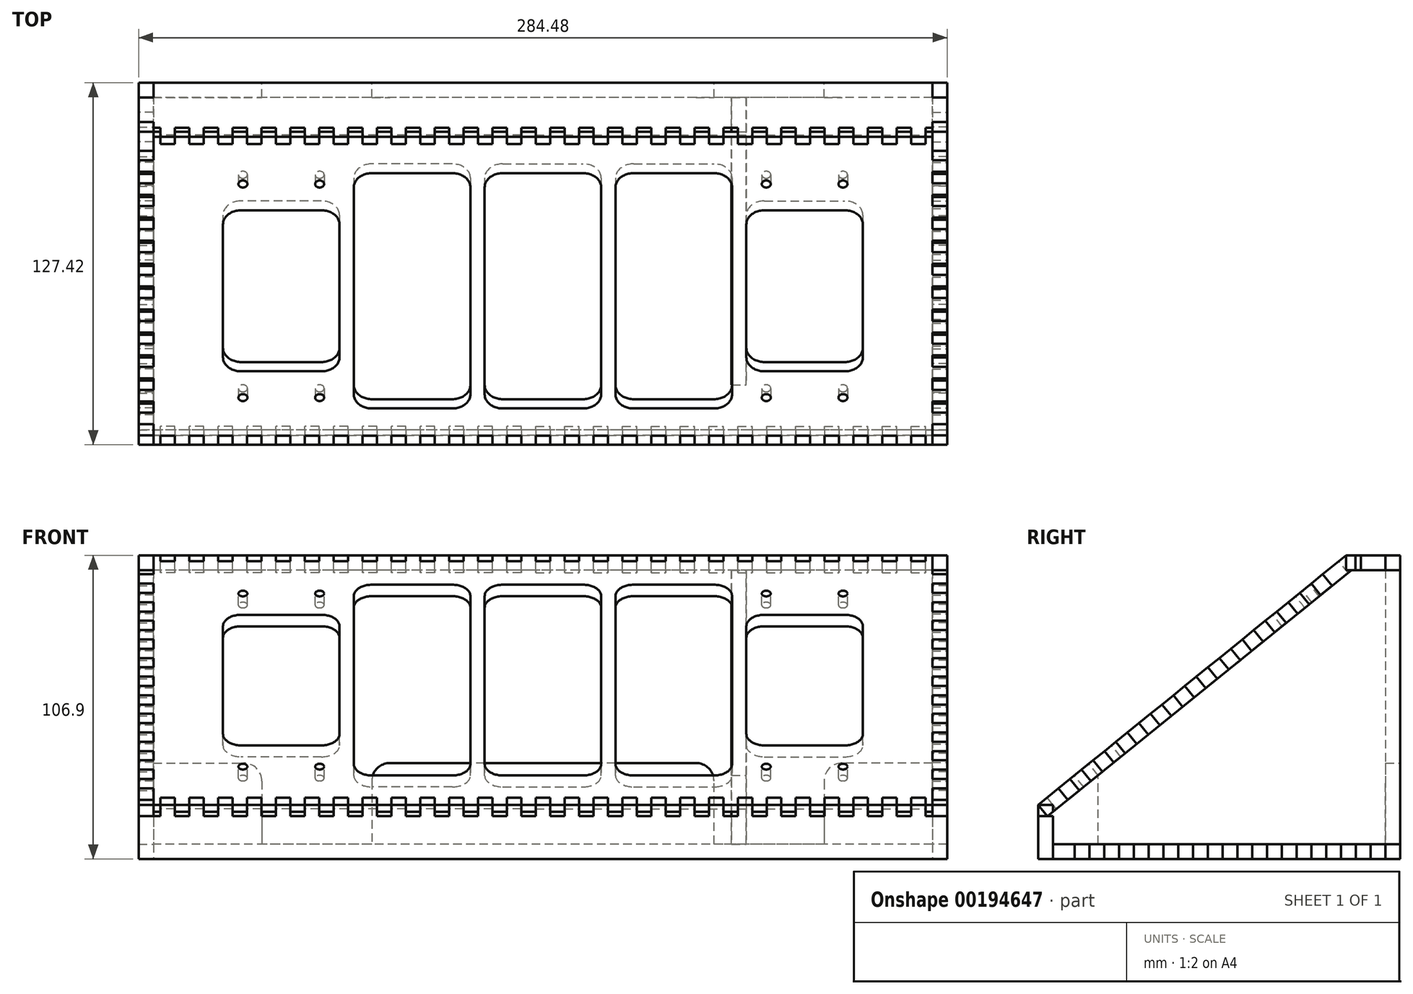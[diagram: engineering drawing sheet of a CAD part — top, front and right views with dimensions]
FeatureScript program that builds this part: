
annotation { "Feature Type Name" : "Feature", "Feature Type Description" : "" }
export const myFeature = defineFeature(function(context is Context, id is Id, definition is map)
    precondition{}
    {
        {
            var Q0;
            Q0=qCreatedBy(makeId("Right.planeOp"),FACE);
            var sketch = newSketch(context, id + "F0", { "sketchPlane" : qUnion([Q0])});
            skLineSegment(sketch, "E0.bottom", {"start": v(61.11, -2.6) * mm, "end": v(-61.11, -2.6) * mm});
            skLineSegment(sketch, "E0.top", {"start": v(61.11, 2.6) * mm, "end": v(-61.11, 2.6) * mm});
            skLineSegment(sketch, "E0.left", {"start": v(61.11, -2.6) * mm, "end": v(61.11, 2.6) * mm});
            skLineSegment(sketch, "E0.right", {"start": v(-61.11, -2.6) * mm, "end": v(-61.11, 2.6) * mm});
            skPoint(sketch, "E0.middle", {"position": v(0, 0) * mm});
            skLineSegment(sketch, "E1.bottom", {"start": v(-66.31, 16.45) * mm, "end": v(42.06, 104.3) * mm});
            skLineSegment(sketch, "E1.top", {"start": v(-63.04, 12.41) * mm, "end": v(45.34, 100.26) * mm});
            skLineSegment(sketch, "E1.left", {"start": v(-66.31, 16.45) * mm, "end": v(-63.04, 12.41) * mm});
            skLineSegment(sketch, "E1.right", {"start": v(42.06, 104.3) * mm, "end": v(45.34, 100.26) * mm});
            skLineSegment(sketch, "E2.bottom", {"start": v(-66.31, 16.45) * mm, "end": v(-61.11, 16.45) * mm});
            skLineSegment(sketch, "E2.top", {"start": v(-66.31, -2.6) * mm, "end": v(-61.11, -2.6) * mm});
            skLineSegment(sketch, "E2.left", {"start": v(-66.31, 16.45) * mm, "end": v(-66.31, -2.6) * mm});
            skLineSegment(sketch, "E2.right", {"start": v(-61.11, 16.45) * mm, "end": v(-61.11, -2.6) * mm});
            skLineSegment(sketch, "E3.bottom", {"start": v(-63.68, 26.3) * mm, "end": v(31.87, 103.76) * mm, "construction": true});
            skLineSegment(sketch, "E3.top", {"start": v(-59.9, 21.65) * mm, "end": v(35.65, 99.1) * mm, "construction": true});
            skLineSegment(sketch, "E3.left", {"start": v(-63.68, 26.3) * mm, "end": v(-59.9, 21.65) * mm, "construction": true});
            skLineSegment(sketch, "E3.right", {"start": v(31.87, 103.76) * mm, "end": v(35.65, 99.1) * mm, "construction": true});
            skLineSegment(sketch, "E4.bottom", {"start": v(42.06, 104.3) * mm, "end": v(61.11, 104.3) * mm});
            skLineSegment(sketch, "E4.top", {"start": v(42.06, 99.1) * mm, "end": v(61.11, 99.1) * mm});
            skLineSegment(sketch, "E4.left", {"start": v(42.06, 104.3) * mm, "end": v(42.06, 99.1) * mm});
            skLineSegment(sketch, "E4.right", {"start": v(61.11, 104.3) * mm, "end": v(61.11, 99.1) * mm});
            skLineSegment(sketch, "E5.bottom", {"start": v(61.11, 99.1) * mm, "end": v(55.91, 99.1) * mm});
            skLineSegment(sketch, "E5.top", {"start": v(61.11, 2.6) * mm, "end": v(55.91, 2.6) * mm});
            skLineSegment(sketch, "E5.left", {"start": v(61.11, 99.1) * mm, "end": v(61.11, 2.6) * mm});
            skLineSegment(sketch, "E5.right", {"start": v(55.91, 99.1) * mm, "end": v(55.91, 2.6) * mm});
            skLineSegment(sketch, "E6.bottom", {"start": v(-42.32, 43.63) * mm, "end": v(10.51, 86.44) * mm, "construction": true});
            skLineSegment(sketch, "E6.top", {"start": v(-15.24, 10.22) * mm, "end": v(37.59, 53.04) * mm, "construction": true});
            skLineSegment(sketch, "E6.left", {"start": v(-42.32, 43.63) * mm, "end": v(-15.24, 10.22) * mm, "construction": true});
            skLineSegment(sketch, "E6.right", {"start": v(10.51, 86.44) * mm, "end": v(37.59, 53.04) * mm, "construction": true});
            skPoint(sketch, "E7", {"position": v(-15.9, 65.03) * mm});
            skLineSegment(sketch, "E8", {"start": v(-63.18, 19) * mm, "end": v(-59.9, 14.95) * mm, "construction": true});
            skLineSegment(sketch, "E9", {"start": v(-66.31, 12.41) * mm, "end": v(-61.11, 12.41) * mm, "construction": true});
            skLineSegment(sketch, "E10", {"start": v(45.34, 104.3) * mm, "end": v(45.34, 99.1) * mm, "construction": true});
            skLineSegment(sketch, "E11", {"start": v(39.52, 102.23) * mm, "end": v(42.8, 98.2) * mm, "construction": true});
            skSolve(sketch);
        }
        {
            var Q0;
            Q0=qCreatedBy(makeId("Right.planeOp"),FACE);
            var sketch = newSketch(context, id + "F1", { "sketchPlane" : qUnion([Q0])});
            skLineSegment(sketch, "E12.0", {"start": v(-63.04, 12.41) * mm, "end": v(45.34, 100.26) * mm});
            skLineSegment(sketch, "E12.1", {"start": v(-66.31, 16.45) * mm, "end": v(-63.04, 12.41) * mm});
            skLineSegment(sketch, "E12.2", {"start": v(-66.31, 16.45) * mm, "end": v(42.06, 104.3) * mm});
            skLineSegment(sketch, "E12.3", {"start": v(42.06, 104.3) * mm, "end": v(45.34, 100.26) * mm});
            skSolve(sketch);
        }
        {
            var Q0;
            Q0 = qSketchRegion(id + "F1", true);
            extrude(context, id + "F2", {"entities" : qUnion([Q0]), "depth" : 142.24 * mm, "hasSecondDirection" : true, "secondDirectionOppositeDirection" : true, "secondDirectionDepth" : 142.24 * mm});
        }
        {
            var Q0;
            Q0=makeQuery(id+"F2.opExtrude","SWEPT_FACE",FACE,{"disambiguationData":[OSD([sQuery(id+"F1.wireOp",EDGE,"E12.2")])]});
            var sketch = newSketch(context, id + "F3", { "sketchPlane" : qUnion([Q0])});
            skLineSegment(sketch, "E13.bottom", {"start": v(-2.54, -41.16) * mm, "end": v(2.54, -41.16) * mm});
            skLineSegment(sketch, "E13.top", {"start": v(-2.54, -37.12) * mm, "end": v(2.54, -37.12) * mm});
            skLineSegment(sketch, "E13.left", {"start": v(2.54, -41.16) * mm, "end": v(2.54, -37.12) * mm});
            skLineSegment(sketch, "E13.right", {"start": v(-2.54, -41.16) * mm, "end": v(-2.54, -37.12) * mm});
            skPoint(sketch, "E14", {"position": v(0, -37.12) * mm});
            skLineSegment(sketch, "E15.1.0.0", {"start": v(7.62, -41.16) * mm, "end": v(7.62, -37.12) * mm});
            skLineSegment(sketch, "E15.1.0.1", {"start": v(12.7, -41.16) * mm, "end": v(12.7, -37.12) * mm});
            skLineSegment(sketch, "E15.1.0.2", {"start": v(7.62, -37.12) * mm, "end": v(12.7, -37.12) * mm});
            skLineSegment(sketch, "E15.1.0.3", {"start": v(7.62, -41.16) * mm, "end": v(12.7, -41.16) * mm});
            skLineSegment(sketch, "E15.2.0.0", {"start": v(17.78, -41.16) * mm, "end": v(17.78, -37.12) * mm});
            skLineSegment(sketch, "E15.2.0.1", {"start": v(22.86, -41.16) * mm, "end": v(22.86, -37.12) * mm});
            skLineSegment(sketch, "E15.2.0.2", {"start": v(17.78, -37.12) * mm, "end": v(22.86, -37.12) * mm});
            skLineSegment(sketch, "E15.2.0.3", {"start": v(17.78, -41.16) * mm, "end": v(22.86, -41.16) * mm});
            skLineSegment(sketch, "E15.3.0.0", {"start": v(27.94, -41.16) * mm, "end": v(27.94, -37.12) * mm});
            skLineSegment(sketch, "E15.3.0.1", {"start": v(33.02, -41.16) * mm, "end": v(33.02, -37.12) * mm});
            skLineSegment(sketch, "E15.3.0.2", {"start": v(27.94, -37.12) * mm, "end": v(33.02, -37.12) * mm});
            skLineSegment(sketch, "E15.3.0.3", {"start": v(27.94, -41.16) * mm, "end": v(33.02, -41.16) * mm});
            skLineSegment(sketch, "E15.4.0.0", {"start": v(38.1, -41.16) * mm, "end": v(38.1, -37.12) * mm});
            skLineSegment(sketch, "E15.4.0.1", {"start": v(43.18, -41.16) * mm, "end": v(43.18, -37.12) * mm});
            skLineSegment(sketch, "E15.4.0.2", {"start": v(38.1, -37.12) * mm, "end": v(43.18, -37.12) * mm});
            skLineSegment(sketch, "E15.4.0.3", {"start": v(38.1, -41.16) * mm, "end": v(43.18, -41.16) * mm});
            skLineSegment(sketch, "E15.5.0.0", {"start": v(48.26, -41.16) * mm, "end": v(48.26, -37.12) * mm});
            skLineSegment(sketch, "E15.5.0.1", {"start": v(53.34, -41.16) * mm, "end": v(53.34, -37.12) * mm});
            skLineSegment(sketch, "E15.5.0.2", {"start": v(48.26, -37.12) * mm, "end": v(53.34, -37.12) * mm});
            skLineSegment(sketch, "E15.5.0.3", {"start": v(48.26, -41.16) * mm, "end": v(53.34, -41.16) * mm});
            skLineSegment(sketch, "E15.6.0.0", {"start": v(58.42, -41.16) * mm, "end": v(58.42, -37.12) * mm});
            skLineSegment(sketch, "E15.6.0.1", {"start": v(63.5, -41.16) * mm, "end": v(63.5, -37.12) * mm});
            skLineSegment(sketch, "E15.6.0.2", {"start": v(58.42, -37.12) * mm, "end": v(63.5, -37.12) * mm});
            skLineSegment(sketch, "E15.6.0.3", {"start": v(58.42, -41.16) * mm, "end": v(63.5, -41.16) * mm});
            skLineSegment(sketch, "E15.7.0.0", {"start": v(68.58, -41.16) * mm, "end": v(68.58, -37.12) * mm});
            skLineSegment(sketch, "E15.7.0.1", {"start": v(73.66, -41.16) * mm, "end": v(73.66, -37.12) * mm});
            skLineSegment(sketch, "E15.7.0.2", {"start": v(68.58, -37.12) * mm, "end": v(73.66, -37.12) * mm});
            skLineSegment(sketch, "E15.7.0.3", {"start": v(68.58, -41.16) * mm, "end": v(73.66, -41.16) * mm});
            skLineSegment(sketch, "E15.8.0.0", {"start": v(78.74, -41.16) * mm, "end": v(78.74, -37.12) * mm});
            skLineSegment(sketch, "E15.8.0.1", {"start": v(83.82, -41.16) * mm, "end": v(83.82, -37.12) * mm});
            skLineSegment(sketch, "E15.8.0.2", {"start": v(78.74, -37.12) * mm, "end": v(83.82, -37.12) * mm});
            skLineSegment(sketch, "E15.8.0.3", {"start": v(78.74, -41.16) * mm, "end": v(83.82, -41.16) * mm});
            skLineSegment(sketch, "E15.9.0.0", {"start": v(88.9, -41.16) * mm, "end": v(88.9, -37.12) * mm});
            skLineSegment(sketch, "E15.9.0.1", {"start": v(93.98, -41.16) * mm, "end": v(93.98, -37.12) * mm});
            skLineSegment(sketch, "E15.9.0.2", {"start": v(88.9, -37.12) * mm, "end": v(93.98, -37.12) * mm});
            skLineSegment(sketch, "E15.9.0.3", {"start": v(88.9, -41.16) * mm, "end": v(93.98, -41.16) * mm});
            skLineSegment(sketch, "E15.10.0.0", {"start": v(99.06, -41.16) * mm, "end": v(99.06, -37.12) * mm});
            skLineSegment(sketch, "E15.10.0.1", {"start": v(104.14, -41.16) * mm, "end": v(104.14, -37.12) * mm});
            skLineSegment(sketch, "E15.10.0.2", {"start": v(99.06, -37.12) * mm, "end": v(104.14, -37.12) * mm});
            skLineSegment(sketch, "E15.10.0.3", {"start": v(99.06, -41.16) * mm, "end": v(104.14, -41.16) * mm});
            skLineSegment(sketch, "E15.11.0.0", {"start": v(109.22, -41.16) * mm, "end": v(109.22, -37.12) * mm});
            skLineSegment(sketch, "E15.11.0.1", {"start": v(114.3, -41.16) * mm, "end": v(114.3, -37.12) * mm});
            skLineSegment(sketch, "E15.11.0.2", {"start": v(109.22, -37.12) * mm, "end": v(114.3, -37.12) * mm});
            skLineSegment(sketch, "E15.11.0.3", {"start": v(109.22, -41.16) * mm, "end": v(114.3, -41.16) * mm});
            skLineSegment(sketch, "E15.12.0.0", {"start": v(119.38, -41.16) * mm, "end": v(119.38, -37.12) * mm});
            skLineSegment(sketch, "E15.12.0.1", {"start": v(124.46, -41.16) * mm, "end": v(124.46, -37.12) * mm});
            skLineSegment(sketch, "E15.12.0.2", {"start": v(119.38, -37.12) * mm, "end": v(124.46, -37.12) * mm});
            skLineSegment(sketch, "E15.12.0.3", {"start": v(119.38, -41.16) * mm, "end": v(124.46, -41.16) * mm});
            skLineSegment(sketch, "E15.13.0.0", {"start": v(129.54, -41.16) * mm, "end": v(129.54, -37.12) * mm});
            skLineSegment(sketch, "E15.13.0.1", {"start": v(134.62, -41.16) * mm, "end": v(134.62, -37.12) * mm});
            skLineSegment(sketch, "E15.13.0.2", {"start": v(129.54, -37.12) * mm, "end": v(134.62, -37.12) * mm});
            skLineSegment(sketch, "E15.13.0.3", {"start": v(129.54, -41.16) * mm, "end": v(134.62, -41.16) * mm});
            skLineSegment(sketch, "E15.direction1", {"start": v(-2.54, -41.16) * mm, "end": v(7.62, -41.16) * mm, "construction": true});
            skLineSegment(sketch, "E16.MirrorCS", {"start": v(-109.22, -41.16) * mm, "end": v(-109.22, -37.12) * mm});
            skLineSegment(sketch, "E17.MirrorCS", {"start": v(-68.58, -41.16) * mm, "end": v(-68.58, -37.12) * mm});
            skLineSegment(sketch, "E18.MirrorCS", {"start": v(-109.22, -37.12) * mm, "end": v(-114.3, -37.12) * mm});
            skLineSegment(sketch, "E19.MirrorCS", {"start": v(-114.3, -41.16) * mm, "end": v(-114.3, -37.12) * mm});
            skLineSegment(sketch, "E20.MirrorCS", {"start": v(-73.66, -41.16) * mm, "end": v(-73.66, -37.12) * mm});
            skLineSegment(sketch, "E21.MirrorCS", {"start": v(-68.58, -37.12) * mm, "end": v(-73.66, -37.12) * mm});
            skLineSegment(sketch, "E22.MirrorCS", {"start": v(-109.22, -41.16) * mm, "end": v(-114.3, -41.16) * mm});
            skLineSegment(sketch, "E23.MirrorCS", {"start": v(-68.58, -41.16) * mm, "end": v(-73.66, -41.16) * mm});
            skLineSegment(sketch, "E24.MirrorCS", {"start": v(-119.38, -41.16) * mm, "end": v(-119.38, -37.12) * mm});
            skLineSegment(sketch, "E25.MirrorCS", {"start": v(-78.74, -41.16) * mm, "end": v(-78.74, -37.12) * mm});
            skLineSegment(sketch, "E26.MirrorCS", {"start": v(-38.1, -41.16) * mm, "end": v(-38.1, -37.12) * mm});
            skLineSegment(sketch, "E27.MirrorCS", {"start": v(-124.46, -41.16) * mm, "end": v(-124.46, -37.12) * mm});
            skLineSegment(sketch, "E28.MirrorCS", {"start": v(-83.82, -41.16) * mm, "end": v(-83.82, -37.12) * mm});
            skLineSegment(sketch, "E29.MirrorCS", {"start": v(-43.18, -41.16) * mm, "end": v(-43.18, -37.12) * mm});
            skLineSegment(sketch, "E30.MirrorCS", {"start": v(-119.38, -37.12) * mm, "end": v(-124.46, -37.12) * mm});
            skLineSegment(sketch, "E31.MirrorCS", {"start": v(-78.74, -37.12) * mm, "end": v(-83.82, -37.12) * mm});
            skLineSegment(sketch, "E32.MirrorCS", {"start": v(-38.1, -37.12) * mm, "end": v(-43.18, -37.12) * mm});
            skLineSegment(sketch, "E33.MirrorCS", {"start": v(-119.38, -41.16) * mm, "end": v(-124.46, -41.16) * mm});
            skLineSegment(sketch, "E34.MirrorCS", {"start": v(-78.74, -41.16) * mm, "end": v(-83.82, -41.16) * mm});
            skLineSegment(sketch, "E35.MirrorCS", {"start": v(-38.1, -41.16) * mm, "end": v(-43.18, -41.16) * mm});
            skLineSegment(sketch, "E36.MirrorCS", {"start": v(-144.78, -41.16) * mm, "end": v(-144.78, -37.12) * mm});
            skLineSegment(sketch, "E37.MirrorCS", {"start": v(-63.5, -41.16) * mm, "end": v(-63.5, -37.12) * mm});
            skLineSegment(sketch, "E38.MirrorCS", {"start": v(-27.94, -41.16) * mm, "end": v(-27.94, -37.12) * mm});
            skLineSegment(sketch, "E39.MirrorCS", {"start": v(-104.14, -41.16) * mm, "end": v(-104.14, -37.12) * mm});
            skLineSegment(sketch, "E40.MirrorCS", {"start": v(-17.78, -41.16) * mm, "end": v(-22.86, -41.16) * mm});
            skLineSegment(sketch, "E41.MirrorCS", {"start": v(-17.78, -37.12) * mm, "end": v(-22.86, -37.12) * mm});
            skLineSegment(sketch, "E42.MirrorCS", {"start": v(-22.86, -41.16) * mm, "end": v(-22.86, -37.12) * mm});
            skLineSegment(sketch, "E43.MirrorCS", {"start": v(-129.54, -41.16) * mm, "end": v(-129.54, -37.12) * mm});
            skLineSegment(sketch, "E44.MirrorCS", {"start": v(-88.9, -41.16) * mm, "end": v(-88.9, -37.12) * mm});
            skLineSegment(sketch, "E45.MirrorCS", {"start": v(-17.78, -41.16) * mm, "end": v(-17.78, -37.12) * mm});
            skLineSegment(sketch, "E46.MirrorCS", {"start": v(-7.62, -41.16) * mm, "end": v(-12.7, -41.16) * mm});
            skLineSegment(sketch, "E47.MirrorCS", {"start": v(-7.62, -37.12) * mm, "end": v(-12.7, -37.12) * mm});
            skLineSegment(sketch, "E48.MirrorCS", {"start": v(-48.26, -41.16) * mm, "end": v(-48.26, -37.12) * mm});
            skLineSegment(sketch, "E49.MirrorCS", {"start": v(-139.7, -41.16) * mm, "end": v(-139.7, -37.12) * mm});
            skLineSegment(sketch, "E50.MirrorCS", {"start": v(-58.42, -41.16) * mm, "end": v(-58.42, -37.12) * mm});
            skLineSegment(sketch, "E51.MirrorCS", {"start": v(-99.06, -41.16) * mm, "end": v(-99.06, -37.12) * mm});
            skLineSegment(sketch, "E52.MirrorCS", {"start": v(-12.7, -41.16) * mm, "end": v(-12.7, -37.12) * mm});
            skLineSegment(sketch, "E53.MirrorCS", {"start": v(-129.54, -41.16) * mm, "end": v(-134.62, -41.16) * mm});
            skLineSegment(sketch, "E54.MirrorCS", {"start": v(-7.62, -41.16) * mm, "end": v(-7.62, -37.12) * mm});
            skLineSegment(sketch, "E55.MirrorCS", {"start": v(-48.26, -41.16) * mm, "end": v(-53.34, -41.16) * mm});
            skLineSegment(sketch, "E56.MirrorCS", {"start": v(-88.9, -41.16) * mm, "end": v(-93.98, -41.16) * mm});
            skLineSegment(sketch, "E57.MirrorCS", {"start": v(-139.7, -41.16) * mm, "end": v(-144.78, -41.16) * mm});
            skLineSegment(sketch, "E58.MirrorCS", {"start": v(-58.42, -41.16) * mm, "end": v(-63.5, -41.16) * mm});
            skLineSegment(sketch, "E59.MirrorCS", {"start": v(-99.06, -41.16) * mm, "end": v(-104.14, -41.16) * mm});
            skLineSegment(sketch, "E60.MirrorCS", {"start": v(-48.26, -37.12) * mm, "end": v(-53.34, -37.12) * mm});
            skLineSegment(sketch, "E61.MirrorCS", {"start": v(-88.9, -37.12) * mm, "end": v(-93.98, -37.12) * mm});
            skLineSegment(sketch, "E62.MirrorCS", {"start": v(-27.94, -41.16) * mm, "end": v(-33.02, -41.16) * mm});
            skLineSegment(sketch, "E63.MirrorCS", {"start": v(-139.7, -37.12) * mm, "end": v(-144.78, -37.12) * mm});
            skLineSegment(sketch, "E64.MirrorCS", {"start": v(-129.54, -37.12) * mm, "end": v(-134.62, -37.12) * mm});
            skLineSegment(sketch, "E65.MirrorCS", {"start": v(-27.94, -37.12) * mm, "end": v(-33.02, -37.12) * mm});
            skLineSegment(sketch, "E66.MirrorCS", {"start": v(-93.98, -41.16) * mm, "end": v(-93.98, -37.12) * mm});
            skLineSegment(sketch, "E67.MirrorCS", {"start": v(-53.34, -41.16) * mm, "end": v(-53.34, -37.12) * mm});
            skLineSegment(sketch, "E68.MirrorCS", {"start": v(-134.62, -41.16) * mm, "end": v(-134.62, -37.12) * mm});
            skLineSegment(sketch, "E69.MirrorCS", {"start": v(-99.06, -37.12) * mm, "end": v(-104.14, -37.12) * mm});
            skLineSegment(sketch, "E70.MirrorCS", {"start": v(-33.02, -41.16) * mm, "end": v(-33.02, -37.12) * mm});
            skLineSegment(sketch, "E71.MirrorCS", {"start": v(-58.42, -37.12) * mm, "end": v(-63.5, -37.12) * mm});
            skLineSegment(sketch, "E72", {"start": v(-142.24, 28.6) * mm, "end": v(142.24, 28.6) * mm, "construction": true});
            skLineSegment(sketch, "E73.bottom", {"start": v(-2.54, 98.35) * mm, "end": v(2.54, 98.35) * mm});
            skLineSegment(sketch, "E73.top", {"start": v(-2.54, 95.07) * mm, "end": v(2.54, 95.07) * mm});
            skLineSegment(sketch, "E73.left", {"start": v(-2.54, 98.35) * mm, "end": v(-2.54, 95.07) * mm});
            skLineSegment(sketch, "E73.right", {"start": v(2.54, 98.35) * mm, "end": v(2.54, 95.07) * mm});
            skPoint(sketch, "E74", {"position": v(0, 95.07) * mm});
            skLineSegment(sketch, "E75.0.14.0", {"start": v(139.7, -41.16) * mm, "end": v(139.7, -37.12) * mm});
            skLineSegment(sketch, "E75.3.14.0", {"start": v(144.78, -41.16) * mm, "end": v(144.78, -37.12) * mm});
            skLineSegment(sketch, "E75.6.14.0", {"start": v(139.7, -37.12) * mm, "end": v(144.78, -37.12) * mm});
            skLineSegment(sketch, "E75.9.14.0", {"start": v(139.7, -41.16) * mm, "end": v(144.78, -41.16) * mm});
            skLineSegment(sketch, "E76.1.0.0", {"start": v(12.7, 98.35) * mm, "end": v(12.7, 95.07) * mm});
            skLineSegment(sketch, "E76.1.0.1", {"start": v(7.62, 98.35) * mm, "end": v(12.7, 98.35) * mm});
            skLineSegment(sketch, "E76.1.0.2", {"start": v(7.62, 98.35) * mm, "end": v(7.62, 95.07) * mm});
            skLineSegment(sketch, "E76.1.0.3", {"start": v(7.62, 95.07) * mm, "end": v(12.7, 95.07) * mm});
            skLineSegment(sketch, "E76.2.0.0", {"start": v(22.86, 98.35) * mm, "end": v(22.86, 95.07) * mm});
            skLineSegment(sketch, "E76.2.0.1", {"start": v(17.78, 98.35) * mm, "end": v(22.86, 98.35) * mm});
            skLineSegment(sketch, "E76.2.0.2", {"start": v(17.78, 98.35) * mm, "end": v(17.78, 95.07) * mm});
            skLineSegment(sketch, "E76.2.0.3", {"start": v(17.78, 95.07) * mm, "end": v(22.86, 95.07) * mm});
            skLineSegment(sketch, "E76.3.0.0", {"start": v(33.02, 98.35) * mm, "end": v(33.02, 95.07) * mm});
            skLineSegment(sketch, "E76.3.0.1", {"start": v(27.94, 98.35) * mm, "end": v(33.02, 98.35) * mm});
            skLineSegment(sketch, "E76.3.0.2", {"start": v(27.94, 98.35) * mm, "end": v(27.94, 95.07) * mm});
            skLineSegment(sketch, "E76.3.0.3", {"start": v(27.94, 95.07) * mm, "end": v(33.02, 95.07) * mm});
            skLineSegment(sketch, "E76.4.0.0", {"start": v(43.18, 98.35) * mm, "end": v(43.18, 95.07) * mm});
            skLineSegment(sketch, "E76.4.0.1", {"start": v(38.1, 98.35) * mm, "end": v(43.18, 98.35) * mm});
            skLineSegment(sketch, "E76.4.0.2", {"start": v(38.1, 98.35) * mm, "end": v(38.1, 95.07) * mm});
            skLineSegment(sketch, "E76.4.0.3", {"start": v(38.1, 95.07) * mm, "end": v(43.18, 95.07) * mm});
            skLineSegment(sketch, "E76.5.0.0", {"start": v(53.34, 98.35) * mm, "end": v(53.34, 95.07) * mm});
            skLineSegment(sketch, "E76.5.0.1", {"start": v(48.26, 98.35) * mm, "end": v(53.34, 98.35) * mm});
            skLineSegment(sketch, "E76.5.0.2", {"start": v(48.26, 98.35) * mm, "end": v(48.26, 95.07) * mm});
            skLineSegment(sketch, "E76.5.0.3", {"start": v(48.26, 95.07) * mm, "end": v(53.34, 95.07) * mm});
            skLineSegment(sketch, "E76.6.0.0", {"start": v(63.5, 98.35) * mm, "end": v(63.5, 95.07) * mm});
            skLineSegment(sketch, "E76.6.0.1", {"start": v(58.42, 98.35) * mm, "end": v(63.5, 98.35) * mm});
            skLineSegment(sketch, "E76.6.0.2", {"start": v(58.42, 98.35) * mm, "end": v(58.42, 95.07) * mm});
            skLineSegment(sketch, "E76.6.0.3", {"start": v(58.42, 95.07) * mm, "end": v(63.5, 95.07) * mm});
            skLineSegment(sketch, "E76.7.0.0", {"start": v(73.66, 98.35) * mm, "end": v(73.66, 95.07) * mm});
            skLineSegment(sketch, "E76.7.0.1", {"start": v(68.58, 98.35) * mm, "end": v(73.66, 98.35) * mm});
            skLineSegment(sketch, "E76.7.0.2", {"start": v(68.58, 98.35) * mm, "end": v(68.58, 95.07) * mm});
            skLineSegment(sketch, "E76.7.0.3", {"start": v(68.58, 95.07) * mm, "end": v(73.66, 95.07) * mm});
            skLineSegment(sketch, "E76.8.0.0", {"start": v(83.82, 98.35) * mm, "end": v(83.82, 95.07) * mm});
            skLineSegment(sketch, "E76.8.0.1", {"start": v(78.74, 98.35) * mm, "end": v(83.82, 98.35) * mm});
            skLineSegment(sketch, "E76.8.0.2", {"start": v(78.74, 98.35) * mm, "end": v(78.74, 95.07) * mm});
            skLineSegment(sketch, "E76.8.0.3", {"start": v(78.74, 95.07) * mm, "end": v(83.82, 95.07) * mm});
            skLineSegment(sketch, "E76.9.0.0", {"start": v(93.98, 98.35) * mm, "end": v(93.98, 95.07) * mm});
            skLineSegment(sketch, "E76.9.0.1", {"start": v(88.9, 98.35) * mm, "end": v(93.98, 98.35) * mm});
            skLineSegment(sketch, "E76.9.0.2", {"start": v(88.9, 98.35) * mm, "end": v(88.9, 95.07) * mm});
            skLineSegment(sketch, "E76.9.0.3", {"start": v(88.9, 95.07) * mm, "end": v(93.98, 95.07) * mm});
            skLineSegment(sketch, "E76.10.0.0", {"start": v(104.14, 98.35) * mm, "end": v(104.14, 95.07) * mm});
            skLineSegment(sketch, "E76.10.0.1", {"start": v(99.06, 98.35) * mm, "end": v(104.14, 98.35) * mm});
            skLineSegment(sketch, "E76.10.0.2", {"start": v(99.06, 98.35) * mm, "end": v(99.06, 95.07) * mm});
            skLineSegment(sketch, "E76.10.0.3", {"start": v(99.06, 95.07) * mm, "end": v(104.14, 95.07) * mm});
            skLineSegment(sketch, "E76.11.0.0", {"start": v(114.3, 98.35) * mm, "end": v(114.3, 95.07) * mm});
            skLineSegment(sketch, "E76.11.0.1", {"start": v(109.22, 98.35) * mm, "end": v(114.3, 98.35) * mm});
            skLineSegment(sketch, "E76.11.0.2", {"start": v(109.22, 98.35) * mm, "end": v(109.22, 95.07) * mm});
            skLineSegment(sketch, "E76.11.0.3", {"start": v(109.22, 95.07) * mm, "end": v(114.3, 95.07) * mm});
            skLineSegment(sketch, "E76.12.0.0", {"start": v(124.46, 98.35) * mm, "end": v(124.46, 95.07) * mm});
            skLineSegment(sketch, "E76.12.0.1", {"start": v(119.38, 98.35) * mm, "end": v(124.46, 98.35) * mm});
            skLineSegment(sketch, "E76.12.0.2", {"start": v(119.38, 98.35) * mm, "end": v(119.38, 95.07) * mm});
            skLineSegment(sketch, "E76.12.0.3", {"start": v(119.38, 95.07) * mm, "end": v(124.46, 95.07) * mm});
            skLineSegment(sketch, "E76.13.0.0", {"start": v(134.62, 98.35) * mm, "end": v(134.62, 95.07) * mm});
            skLineSegment(sketch, "E76.13.0.1", {"start": v(129.54, 98.35) * mm, "end": v(134.62, 98.35) * mm});
            skLineSegment(sketch, "E76.13.0.2", {"start": v(129.54, 98.35) * mm, "end": v(129.54, 95.07) * mm});
            skLineSegment(sketch, "E76.13.0.3", {"start": v(129.54, 95.07) * mm, "end": v(134.62, 95.07) * mm});
            skLineSegment(sketch, "E76.14.0.0", {"start": v(144.78, 98.35) * mm, "end": v(144.78, 95.07) * mm});
            skLineSegment(sketch, "E76.14.0.1", {"start": v(139.7, 98.35) * mm, "end": v(144.78, 98.35) * mm});
            skLineSegment(sketch, "E76.14.0.2", {"start": v(139.7, 98.35) * mm, "end": v(139.7, 95.07) * mm});
            skLineSegment(sketch, "E76.14.0.3", {"start": v(139.7, 95.07) * mm, "end": v(144.78, 95.07) * mm});
            skLineSegment(sketch, "E76.direction1", {"start": v(-2.54, 95.07) * mm, "end": v(7.62, 95.07) * mm, "construction": true});
            skLineSegment(sketch, "E77.MirrorCS", {"start": v(-119.38, 95.07) * mm, "end": v(-124.46, 95.07) * mm});
            skLineSegment(sketch, "E78.MirrorCS", {"start": v(-68.58, 98.35) * mm, "end": v(-73.66, 98.35) * mm});
            skLineSegment(sketch, "E79.MirrorCS", {"start": v(-78.74, 98.35) * mm, "end": v(-78.74, 95.07) * mm});
            skLineSegment(sketch, "E80.MirrorCS", {"start": v(-27.94, 98.35) * mm, "end": v(-33.02, 98.35) * mm});
            skLineSegment(sketch, "E81.MirrorCS", {"start": v(-38.1, 98.35) * mm, "end": v(-38.1, 95.07) * mm});
            skLineSegment(sketch, "E82.MirrorCS", {"start": v(-27.94, 95.07) * mm, "end": v(-33.02, 95.07) * mm});
            skLineSegment(sketch, "E83.MirrorCS", {"start": v(-27.94, 98.35) * mm, "end": v(-27.94, 95.07) * mm});
            skLineSegment(sketch, "E84.MirrorCS", {"start": v(-68.58, 98.35) * mm, "end": v(-68.58, 95.07) * mm});
            skLineSegment(sketch, "E85.MirrorCS", {"start": v(-88.9, 98.35) * mm, "end": v(-88.9, 95.07) * mm});
            skLineSegment(sketch, "E86.MirrorCS", {"start": v(-129.54, 98.35) * mm, "end": v(-129.54, 95.07) * mm});
            skLineSegment(sketch, "E87.MirrorCS", {"start": v(-109.22, 98.35) * mm, "end": v(-109.22, 95.07) * mm});
            skLineSegment(sketch, "E88.MirrorCS", {"start": v(-124.46, 98.35) * mm, "end": v(-124.46, 95.07) * mm});
            skLineSegment(sketch, "E89.MirrorCS", {"start": v(-83.82, 98.35) * mm, "end": v(-83.82, 95.07) * mm});
            skLineSegment(sketch, "E90.MirrorCS", {"start": v(-43.18, 98.35) * mm, "end": v(-43.18, 95.07) * mm});
            skLineSegment(sketch, "E91.MirrorCS", {"start": v(-22.86, 98.35) * mm, "end": v(-22.86, 95.07) * mm});
            skLineSegment(sketch, "E92.MirrorCS", {"start": v(-48.26, 95.07) * mm, "end": v(-53.34, 95.07) * mm});
            skLineSegment(sketch, "E93.MirrorCS", {"start": v(-129.54, 95.07) * mm, "end": v(-134.62, 95.07) * mm});
            skLineSegment(sketch, "E94.MirrorCS", {"start": v(-88.9, 95.07) * mm, "end": v(-93.98, 95.07) * mm});
            skLineSegment(sketch, "E95.MirrorCS", {"start": v(-99.06, 98.35) * mm, "end": v(-104.14, 98.35) * mm});
            skLineSegment(sketch, "E96.MirrorCS", {"start": v(-48.26, 98.35) * mm, "end": v(-53.34, 98.35) * mm});
            skLineSegment(sketch, "E97.MirrorCS", {"start": v(-88.9, 98.35) * mm, "end": v(-93.98, 98.35) * mm});
            skLineSegment(sketch, "E98.MirrorCS", {"start": v(-7.62, 98.35) * mm, "end": v(-12.7, 98.35) * mm});
            skLineSegment(sketch, "E99.MirrorCS", {"start": v(-7.62, 95.07) * mm, "end": v(-12.7, 95.07) * mm});
            skLineSegment(sketch, "E100.MirrorCS", {"start": v(-119.38, 98.35) * mm, "end": v(-124.46, 98.35) * mm});
            skLineSegment(sketch, "E101.MirrorCS", {"start": v(-58.42, 98.35) * mm, "end": v(-58.42, 95.07) * mm});
            skLineSegment(sketch, "E102.MirrorCS", {"start": v(-63.5, 98.35) * mm, "end": v(-63.5, 95.07) * mm});
            skLineSegment(sketch, "E103.MirrorCS", {"start": v(-93.98, 98.35) * mm, "end": v(-93.98, 95.07) * mm});
            skLineSegment(sketch, "E104.MirrorCS", {"start": v(-134.62, 98.35) * mm, "end": v(-134.62, 95.07) * mm});
            skLineSegment(sketch, "E105.MirrorCS", {"start": v(-53.34, 98.35) * mm, "end": v(-53.34, 95.07) * mm});
            skLineSegment(sketch, "E106.MirrorCS", {"start": v(-38.1, 95.07) * mm, "end": v(-43.18, 95.07) * mm});
            skLineSegment(sketch, "E107.MirrorCS", {"start": v(-58.42, 98.35) * mm, "end": v(-63.5, 98.35) * mm});
            skLineSegment(sketch, "E108.MirrorCS", {"start": v(-114.3, 98.35) * mm, "end": v(-114.3, 95.07) * mm});
            skLineSegment(sketch, "E109.MirrorCS", {"start": v(-7.62, 98.35) * mm, "end": v(-7.62, 95.07) * mm});
            skLineSegment(sketch, "E110.MirrorCS", {"start": v(-68.58, 95.07) * mm, "end": v(-73.66, 95.07) * mm});
            skLineSegment(sketch, "E111.MirrorCS", {"start": v(-144.78, 98.35) * mm, "end": v(-144.78, 95.07) * mm});
            skLineSegment(sketch, "E112.MirrorCS", {"start": v(-38.1, 98.35) * mm, "end": v(-43.18, 98.35) * mm});
            skLineSegment(sketch, "E113.MirrorCS", {"start": v(-78.74, 98.35) * mm, "end": v(-83.82, 98.35) * mm});
            skLineSegment(sketch, "E114.MirrorCS", {"start": v(-48.26, 98.35) * mm, "end": v(-48.26, 95.07) * mm});
            skLineSegment(sketch, "E115.MirrorCS", {"start": v(-119.38, 98.35) * mm, "end": v(-119.38, 95.07) * mm});
            skLineSegment(sketch, "E116.MirrorCS", {"start": v(-33.02, 98.35) * mm, "end": v(-33.02, 95.07) * mm});
            skLineSegment(sketch, "E117.MirrorCS", {"start": v(-78.74, 95.07) * mm, "end": v(-83.82, 95.07) * mm});
            skLineSegment(sketch, "E118.MirrorCS", {"start": v(-129.54, 98.35) * mm, "end": v(-134.62, 98.35) * mm});
            skLineSegment(sketch, "E119.MirrorCS", {"start": v(-12.7, 98.35) * mm, "end": v(-12.7, 95.07) * mm});
            skLineSegment(sketch, "E120.MirrorCS", {"start": v(-73.66, 98.35) * mm, "end": v(-73.66, 95.07) * mm});
            skLineSegment(sketch, "E121.MirrorCS", {"start": v(-17.78, 98.35) * mm, "end": v(-17.78, 95.07) * mm});
            skLineSegment(sketch, "E122.MirrorCS", {"start": v(-99.06, 98.35) * mm, "end": v(-99.06, 95.07) * mm});
            skLineSegment(sketch, "E123.MirrorCS", {"start": v(-99.06, 95.07) * mm, "end": v(-104.14, 95.07) * mm});
            skLineSegment(sketch, "E124.MirrorCS", {"start": v(-58.42, 95.07) * mm, "end": v(-63.5, 95.07) * mm});
            skLineSegment(sketch, "E125.MirrorCS", {"start": v(-17.78, 95.07) * mm, "end": v(-22.86, 95.07) * mm});
            skLineSegment(sketch, "E126.MirrorCS", {"start": v(-139.7, 98.35) * mm, "end": v(-139.7, 95.07) * mm});
            skLineSegment(sketch, "E127.MirrorCS", {"start": v(-17.78, 98.35) * mm, "end": v(-22.86, 98.35) * mm});
            skLineSegment(sketch, "E128.MirrorCS", {"start": v(-104.14, 98.35) * mm, "end": v(-104.14, 95.07) * mm});
            skLineSegment(sketch, "E129.MirrorCS", {"start": v(-109.22, 98.35) * mm, "end": v(-114.3, 98.35) * mm});
            skLineSegment(sketch, "E130.MirrorCS", {"start": v(-109.22, 95.07) * mm, "end": v(-114.3, 95.07) * mm});
            skLineSegment(sketch, "E131.MirrorCS", {"start": v(-139.7, 98.35) * mm, "end": v(-144.78, 98.35) * mm});
            skLineSegment(sketch, "E132.MirrorCS", {"start": v(-139.7, 95.07) * mm, "end": v(-144.78, 95.07) * mm});
            skSolve(sketch);
        }
        {
            var Q0;
            Q0 = qSketchRegion(id + "F3", true);
            extrude(context, id + "F4", {"entities" : qUnion([Q0]), "operationType" : NewBodyOperationType.REMOVE, "endBound" : BoundingType.THROUGH_ALL, "oppositeDirection" : true, "depth" : 25.4 * mm});
        }
        {
            var Q0;
            Q0=qCreatedBy(makeId("Right.planeOp"),FACE);
            var sketch = newSketch(context, id + "F5", { "sketchPlane" : qUnion([Q0])});
            skLineSegment(sketch, "E133.0", {"start": v(-61.11, 16.45) * mm, "end": v(-61.11, -2.6) * mm});
            skLineSegment(sketch, "E133.1", {"start": v(-66.31, -2.6) * mm, "end": v(-61.11, -2.6) * mm});
            skLineSegment(sketch, "E133.2", {"start": v(-66.31, 16.45) * mm, "end": v(-66.31, -2.6) * mm});
            skLineSegment(sketch, "E133.3", {"start": v(-66.31, 16.45) * mm, "end": v(-61.11, 16.45) * mm});
            skSolve(sketch);
        }
        {
            var Q0;
            Q0 = qSketchRegion(id + "F5", true);
            extrude(context, id + "F6", {"entities" : qUnion([Q0]), "depth" : 142.24 * mm, "hasSecondDirection" : true, "secondDirectionOppositeDirection" : true, "secondDirectionDepth" : 142.24 * mm});
        }
        {
            var Q0;
            Q0=makeQuery(id+"F6.opExtrude","SWEPT_FACE",FACE,{"disambiguationData":[OSD([sQuery(id+"F5.wireOp",EDGE,"E133.2")])]});
            var sketch = newSketch(context, id + "F7", { "sketchPlane" : qUnion([Q0])});
            skLineSegment(sketch, "E134.bottom", {"start": v(2.54, 16.45) * mm, "end": v(7.62, 16.45) * mm});
            skLineSegment(sketch, "E134.top", {"start": v(2.54, 12.46) * mm, "end": v(7.62, 12.46) * mm});
            skLineSegment(sketch, "E134.left", {"start": v(2.54, 16.45) * mm, "end": v(2.54, 12.46) * mm});
            skLineSegment(sketch, "E134.right", {"start": v(7.62, 16.45) * mm, "end": v(7.62, 12.46) * mm});
            skLineSegment(sketch, "E135", {"start": v(2.54, 16.45) * mm, "end": v(-2.54, 16.45) * mm, "construction": true});
            skLineSegment(sketch, "E136.1.0.0", {"start": v(17.78, 16.45) * mm, "end": v(17.78, 12.46) * mm});
            skLineSegment(sketch, "E136.1.0.1", {"start": v(12.7, 16.45) * mm, "end": v(12.7, 12.46) * mm});
            skLineSegment(sketch, "E136.1.0.2", {"start": v(12.7, 12.46) * mm, "end": v(17.78, 12.46) * mm});
            skLineSegment(sketch, "E136.1.0.3", {"start": v(12.7, 16.45) * mm, "end": v(17.78, 16.45) * mm});
            skLineSegment(sketch, "E136.2.0.0", {"start": v(27.94, 16.45) * mm, "end": v(27.94, 12.46) * mm});
            skLineSegment(sketch, "E136.2.0.1", {"start": v(22.86, 16.45) * mm, "end": v(22.86, 12.46) * mm});
            skLineSegment(sketch, "E136.2.0.2", {"start": v(22.86, 12.46) * mm, "end": v(27.94, 12.46) * mm});
            skLineSegment(sketch, "E136.2.0.3", {"start": v(22.86, 16.45) * mm, "end": v(27.94, 16.45) * mm});
            skLineSegment(sketch, "E136.3.0.0", {"start": v(38.1, 16.45) * mm, "end": v(38.1, 12.46) * mm});
            skLineSegment(sketch, "E136.3.0.1", {"start": v(33.02, 16.45) * mm, "end": v(33.02, 12.46) * mm});
            skLineSegment(sketch, "E136.3.0.2", {"start": v(33.02, 12.46) * mm, "end": v(38.1, 12.46) * mm});
            skLineSegment(sketch, "E136.3.0.3", {"start": v(33.02, 16.45) * mm, "end": v(38.1, 16.45) * mm});
            skLineSegment(sketch, "E136.4.0.0", {"start": v(48.26, 16.45) * mm, "end": v(48.26, 12.46) * mm});
            skLineSegment(sketch, "E136.4.0.1", {"start": v(43.18, 16.45) * mm, "end": v(43.18, 12.46) * mm});
            skLineSegment(sketch, "E136.4.0.2", {"start": v(43.18, 12.46) * mm, "end": v(48.26, 12.46) * mm});
            skLineSegment(sketch, "E136.4.0.3", {"start": v(43.18, 16.45) * mm, "end": v(48.26, 16.45) * mm});
            skLineSegment(sketch, "E136.5.0.0", {"start": v(58.42, 16.45) * mm, "end": v(58.42, 12.46) * mm});
            skLineSegment(sketch, "E136.5.0.1", {"start": v(53.34, 16.45) * mm, "end": v(53.34, 12.46) * mm});
            skLineSegment(sketch, "E136.5.0.2", {"start": v(53.34, 12.46) * mm, "end": v(58.42, 12.46) * mm});
            skLineSegment(sketch, "E136.5.0.3", {"start": v(53.34, 16.45) * mm, "end": v(58.42, 16.45) * mm});
            skLineSegment(sketch, "E136.6.0.0", {"start": v(68.58, 16.45) * mm, "end": v(68.58, 12.46) * mm});
            skLineSegment(sketch, "E136.6.0.1", {"start": v(63.5, 16.45) * mm, "end": v(63.5, 12.46) * mm});
            skLineSegment(sketch, "E136.6.0.2", {"start": v(63.5, 12.46) * mm, "end": v(68.58, 12.46) * mm});
            skLineSegment(sketch, "E136.6.0.3", {"start": v(63.5, 16.45) * mm, "end": v(68.58, 16.45) * mm});
            skLineSegment(sketch, "E136.7.0.0", {"start": v(78.74, 16.45) * mm, "end": v(78.74, 12.46) * mm});
            skLineSegment(sketch, "E136.7.0.1", {"start": v(73.66, 16.45) * mm, "end": v(73.66, 12.46) * mm});
            skLineSegment(sketch, "E136.7.0.2", {"start": v(73.66, 12.46) * mm, "end": v(78.74, 12.46) * mm});
            skLineSegment(sketch, "E136.7.0.3", {"start": v(73.66, 16.45) * mm, "end": v(78.74, 16.45) * mm});
            skLineSegment(sketch, "E136.8.0.0", {"start": v(88.9, 16.45) * mm, "end": v(88.9, 12.46) * mm});
            skLineSegment(sketch, "E136.8.0.1", {"start": v(83.82, 16.45) * mm, "end": v(83.82, 12.46) * mm});
            skLineSegment(sketch, "E136.8.0.2", {"start": v(83.82, 12.46) * mm, "end": v(88.9, 12.46) * mm});
            skLineSegment(sketch, "E136.8.0.3", {"start": v(83.82, 16.45) * mm, "end": v(88.9, 16.45) * mm});
            skLineSegment(sketch, "E136.9.0.0", {"start": v(99.06, 16.45) * mm, "end": v(99.06, 12.46) * mm});
            skLineSegment(sketch, "E136.9.0.1", {"start": v(93.98, 16.45) * mm, "end": v(93.98, 12.46) * mm});
            skLineSegment(sketch, "E136.9.0.2", {"start": v(93.98, 12.46) * mm, "end": v(99.06, 12.46) * mm});
            skLineSegment(sketch, "E136.9.0.3", {"start": v(93.98, 16.45) * mm, "end": v(99.06, 16.45) * mm});
            skLineSegment(sketch, "E136.10.0.0", {"start": v(109.22, 16.45) * mm, "end": v(109.22, 12.46) * mm});
            skLineSegment(sketch, "E136.10.0.1", {"start": v(104.14, 16.45) * mm, "end": v(104.14, 12.46) * mm});
            skLineSegment(sketch, "E136.10.0.2", {"start": v(104.14, 12.46) * mm, "end": v(109.22, 12.46) * mm});
            skLineSegment(sketch, "E136.10.0.3", {"start": v(104.14, 16.45) * mm, "end": v(109.22, 16.45) * mm});
            skLineSegment(sketch, "E136.11.0.0", {"start": v(119.38, 16.45) * mm, "end": v(119.38, 12.46) * mm});
            skLineSegment(sketch, "E136.11.0.1", {"start": v(114.3, 16.45) * mm, "end": v(114.3, 12.46) * mm});
            skLineSegment(sketch, "E136.11.0.2", {"start": v(114.3, 12.46) * mm, "end": v(119.38, 12.46) * mm});
            skLineSegment(sketch, "E136.11.0.3", {"start": v(114.3, 16.45) * mm, "end": v(119.38, 16.45) * mm});
            skLineSegment(sketch, "E136.12.0.0", {"start": v(129.54, 16.45) * mm, "end": v(129.54, 12.46) * mm});
            skLineSegment(sketch, "E136.12.0.1", {"start": v(124.46, 16.45) * mm, "end": v(124.46, 12.46) * mm});
            skLineSegment(sketch, "E136.12.0.2", {"start": v(124.46, 12.46) * mm, "end": v(129.54, 12.46) * mm});
            skLineSegment(sketch, "E136.12.0.3", {"start": v(124.46, 16.45) * mm, "end": v(129.54, 16.45) * mm});
            skLineSegment(sketch, "E136.13.0.0", {"start": v(139.7, 16.45) * mm, "end": v(139.7, 12.46) * mm, "construction": true});
            skLineSegment(sketch, "E136.13.0.1", {"start": v(134.62, 16.45) * mm, "end": v(134.62, 12.46) * mm});
            skLineSegment(sketch, "E136.13.0.2", {"start": v(134.62, 12.46) * mm, "end": v(139.7, 12.46) * mm});
            skLineSegment(sketch, "E136.13.0.3", {"start": v(134.62, 16.45) * mm, "end": v(139.7, 16.45) * mm});
            skLineSegment(sketch, "E136.direction1", {"start": v(2.54, 12.46) * mm, "end": v(12.7, 12.46) * mm, "construction": true});
            skLineSegment(sketch, "E137.MirrorCS", {"start": v(-2.54, 16.45) * mm, "end": v(-2.54, 12.46) * mm});
            skLineSegment(sketch, "E138.MirrorCS", {"start": v(-2.54, 12.46) * mm, "end": v(-7.62, 12.46) * mm});
            skLineSegment(sketch, "E139.MirrorCS", {"start": v(-134.62, 12.46) * mm, "end": v(-139.7, 12.46) * mm});
            skLineSegment(sketch, "E140.MirrorCS", {"start": v(-53.34, 12.46) * mm, "end": v(-58.42, 12.46) * mm});
            skLineSegment(sketch, "E141.MirrorCS", {"start": v(-93.98, 12.46) * mm, "end": v(-99.06, 12.46) * mm});
            skLineSegment(sketch, "E142.MirrorCS", {"start": v(-33.02, 16.45) * mm, "end": v(-38.1, 16.45) * mm});
            skLineSegment(sketch, "E143.MirrorCS", {"start": v(-73.66, 16.45) * mm, "end": v(-78.74, 16.45) * mm});
            skLineSegment(sketch, "E144.MirrorCS", {"start": v(-114.3, 16.45) * mm, "end": v(-119.38, 16.45) * mm});
            skLineSegment(sketch, "E145.MirrorCS", {"start": v(-53.34, 16.45) * mm, "end": v(-53.34, 12.46) * mm});
            skLineSegment(sketch, "E146.MirrorCS", {"start": v(-73.66, 12.46) * mm, "end": v(-78.74, 12.46) * mm});
            skLineSegment(sketch, "E147.MirrorCS", {"start": v(-93.98, 16.45) * mm, "end": v(-93.98, 12.46) * mm});
            skLineSegment(sketch, "E148.MirrorCS", {"start": v(-114.3, 12.46) * mm, "end": v(-119.38, 12.46) * mm});
            skLineSegment(sketch, "E149.MirrorCS", {"start": v(-134.62, 16.45) * mm, "end": v(-134.62, 12.46) * mm});
            skLineSegment(sketch, "E150.MirrorCS", {"start": v(-58.42, 16.45) * mm, "end": v(-58.42, 12.46) * mm});
            skLineSegment(sketch, "E151.MirrorCS", {"start": v(-73.66, 16.45) * mm, "end": v(-73.66, 12.46) * mm});
            skLineSegment(sketch, "E152.MirrorCS", {"start": v(-99.06, 16.45) * mm, "end": v(-99.06, 12.46) * mm});
            skLineSegment(sketch, "E153.MirrorCS", {"start": v(-114.3, 16.45) * mm, "end": v(-114.3, 12.46) * mm});
            skLineSegment(sketch, "E154.MirrorCS", {"start": v(-139.7, 16.45) * mm, "end": v(-139.7, 12.46) * mm, "construction": true});
            skLineSegment(sketch, "E155.MirrorCS", {"start": v(-63.5, 16.45) * mm, "end": v(-68.58, 16.45) * mm});
            skLineSegment(sketch, "E156.MirrorCS", {"start": v(-104.14, 16.45) * mm, "end": v(-109.22, 16.45) * mm});
            skLineSegment(sketch, "E157.MirrorCS", {"start": v(-43.18, 16.45) * mm, "end": v(-48.26, 16.45) * mm});
            skLineSegment(sketch, "E158.MirrorCS", {"start": v(-83.82, 16.45) * mm, "end": v(-88.9, 16.45) * mm});
            skLineSegment(sketch, "E159.MirrorCS", {"start": v(-78.74, 16.45) * mm, "end": v(-78.74, 12.46) * mm});
            skLineSegment(sketch, "E160.MirrorCS", {"start": v(-124.46, 16.45) * mm, "end": v(-129.54, 16.45) * mm});
            skLineSegment(sketch, "E161.MirrorCS", {"start": v(-119.38, 16.45) * mm, "end": v(-119.38, 12.46) * mm});
            skLineSegment(sketch, "E162.MirrorCS", {"start": v(-63.5, 12.46) * mm, "end": v(-68.58, 12.46) * mm});
            skLineSegment(sketch, "E163.MirrorCS", {"start": v(-104.14, 12.46) * mm, "end": v(-109.22, 12.46) * mm});
            skLineSegment(sketch, "E164.MirrorCS", {"start": v(-43.18, 12.46) * mm, "end": v(-48.26, 12.46) * mm});
            skLineSegment(sketch, "E165.MirrorCS", {"start": v(-83.82, 12.46) * mm, "end": v(-88.9, 12.46) * mm});
            skLineSegment(sketch, "E166.MirrorCS", {"start": v(-124.46, 12.46) * mm, "end": v(-129.54, 12.46) * mm});
            skLineSegment(sketch, "E167.MirrorCS", {"start": v(-63.5, 16.45) * mm, "end": v(-63.5, 12.46) * mm});
            skLineSegment(sketch, "E168.MirrorCS", {"start": v(-104.14, 16.45) * mm, "end": v(-104.14, 12.46) * mm});
            skLineSegment(sketch, "E169.MirrorCS", {"start": v(-68.58, 16.45) * mm, "end": v(-68.58, 12.46) * mm});
            skLineSegment(sketch, "E170.MirrorCS", {"start": v(-109.22, 16.45) * mm, "end": v(-109.22, 12.46) * mm});
            skLineSegment(sketch, "E171.MirrorCS", {"start": v(-43.18, 16.45) * mm, "end": v(-43.18, 12.46) * mm});
            skLineSegment(sketch, "E172.MirrorCS", {"start": v(-83.82, 16.45) * mm, "end": v(-83.82, 12.46) * mm});
            skLineSegment(sketch, "E173.MirrorCS", {"start": v(-124.46, 16.45) * mm, "end": v(-124.46, 12.46) * mm});
            skLineSegment(sketch, "E174.MirrorCS", {"start": v(-134.62, 16.45) * mm, "end": v(-139.7, 16.45) * mm});
            skLineSegment(sketch, "E175.MirrorCS", {"start": v(-53.34, 16.45) * mm, "end": v(-58.42, 16.45) * mm});
            skLineSegment(sketch, "E176.MirrorCS", {"start": v(-93.98, 16.45) * mm, "end": v(-99.06, 16.45) * mm});
            skLineSegment(sketch, "E177.MirrorCS", {"start": v(-22.86, 16.45) * mm, "end": v(-27.94, 16.45) * mm});
            skLineSegment(sketch, "E178.MirrorCS", {"start": v(-22.86, 12.46) * mm, "end": v(-27.94, 12.46) * mm});
            skLineSegment(sketch, "E179.MirrorCS", {"start": v(-22.86, 16.45) * mm, "end": v(-22.86, 12.46) * mm});
            skLineSegment(sketch, "E180.MirrorCS", {"start": v(-27.94, 16.45) * mm, "end": v(-27.94, 12.46) * mm});
            skLineSegment(sketch, "E181.MirrorCS", {"start": v(-12.7, 16.45) * mm, "end": v(-17.78, 16.45) * mm});
            skLineSegment(sketch, "E182.MirrorCS", {"start": v(-12.7, 12.46) * mm, "end": v(-17.78, 12.46) * mm});
            skLineSegment(sketch, "E183.MirrorCS", {"start": v(-12.7, 16.45) * mm, "end": v(-12.7, 12.46) * mm});
            skLineSegment(sketch, "E184.MirrorCS", {"start": v(-17.78, 16.45) * mm, "end": v(-17.78, 12.46) * mm});
            skLineSegment(sketch, "E185.MirrorCS", {"start": v(-7.62, 16.45) * mm, "end": v(-7.62, 12.46) * mm});
            skLineSegment(sketch, "E186.MirrorCS", {"start": v(-2.54, 16.45) * mm, "end": v(-7.62, 16.45) * mm});
            skLineSegment(sketch, "E187.MirrorCS", {"start": v(-33.02, 12.46) * mm, "end": v(-38.1, 12.46) * mm});
            skLineSegment(sketch, "E188.MirrorCS", {"start": v(-33.02, 16.45) * mm, "end": v(-33.02, 12.46) * mm});
            skLineSegment(sketch, "E189.MirrorCS", {"start": v(-38.1, 16.45) * mm, "end": v(-38.1, 12.46) * mm});
            skLineSegment(sketch, "E190.MirrorCS", {"start": v(-48.26, 16.45) * mm, "end": v(-48.26, 12.46) * mm});
            skLineSegment(sketch, "E191.MirrorCS", {"start": v(-129.54, 16.45) * mm, "end": v(-129.54, 12.46) * mm});
            skLineSegment(sketch, "E192.MirrorCS", {"start": v(-88.9, 16.45) * mm, "end": v(-88.9, 12.46) * mm});
            skLineSegment(sketch, "E193", {"start": v(139.7, 16.45) * mm, "end": v(142.24, 16.45) * mm});
            skLineSegment(sketch, "E194", {"start": v(142.24, 16.45) * mm, "end": v(142.24, 12.46) * mm});
            skLineSegment(sketch, "E195", {"start": v(142.24, 12.46) * mm, "end": v(139.7, 12.46) * mm});
            skLineSegment(sketch, "E196", {"start": v(-139.7, 16.45) * mm, "end": v(-142.24, 16.45) * mm});
            skLineSegment(sketch, "E197", {"start": v(-142.24, 16.45) * mm, "end": v(-142.24, 12.46) * mm});
            skLineSegment(sketch, "E198", {"start": v(-142.24, 12.46) * mm, "end": v(-139.7, 12.46) * mm});
            skSolve(sketch);
        }
        {
            var Q0;
            Q0 = qSketchRegion(id + "F7", true);
            var Q1;
            Q1=makeQuery(id+"F6.opExtrude","SWEPT_FACE",FACE,{"disambiguationData":[OSD([sQuery(id+"F5.wireOp",EDGE,"E133.0")])]});
            extrude(context, id + "F8", {"entities" : qUnion([Q0]), "operationType" : NewBodyOperationType.REMOVE, "endBound" : BoundingType.UP_TO_SURFACE, "oppositeDirection" : true, "endBoundEntityFace" : qUnion([Q1]), "depth" : 25.4 * mm});
        }
        {
            var Q0;
            Q0=qCreatedBy(makeId("Right.planeOp"),FACE);
            var sketch = newSketch(context, id + "F9", { "sketchPlane" : qUnion([Q0])});
            skLineSegment(sketch, "E199.0", {"start": v(42.06, 104.3) * mm, "end": v(61.11, 104.3) * mm});
            skLineSegment(sketch, "E199.1", {"start": v(61.11, 104.3) * mm, "end": v(61.11, 99.1) * mm});
            skLineSegment(sketch, "E199.2", {"start": v(42.06, 99.1) * mm, "end": v(61.11, 99.1) * mm});
            skLineSegment(sketch, "E199.3", {"start": v(42.06, 104.3) * mm, "end": v(42.06, 99.1) * mm});
            skSolve(sketch);
        }
        {
            var Q0;
            Q0 = qSketchRegion(id + "F9", true);
            extrude(context, id + "F10", {"entities" : qUnion([Q0]), "depth" : 142.24 * mm, "hasSecondDirection" : true, "secondDirectionOppositeDirection" : true, "secondDirectionDepth" : 142.24 * mm});
        }
        {
            var Q0;
            Q0=makeQuery(id+"F10.opExtrude","SWEPT_FACE",FACE,{"disambiguationData":[OSD([sQuery(id+"F9.wireOp",EDGE,"E199.0")])]});
            var sketch = newSketch(context, id + "F11", { "sketchPlane" : qUnion([Q0])});
            skLineSegment(sketch, "E200.bottom", {"start": v(2.54, 42.06) * mm, "end": v(7.62, 42.06) * mm});
            skLineSegment(sketch, "E200.top", {"start": v(2.54, 45.34) * mm, "end": v(7.62, 45.34) * mm});
            skLineSegment(sketch, "E200.left", {"start": v(2.54, 42.06) * mm, "end": v(2.54, 45.34) * mm});
            skLineSegment(sketch, "E200.right", {"start": v(7.62, 42.06) * mm, "end": v(7.62, 45.34) * mm});
            skLineSegment(sketch, "E201", {"start": v(2.54, 42.06) * mm, "end": v(-2.54, 42.06) * mm});
            skPoint(sketch, "E202", {"position": v(0, 42.06) * mm});
            skLineSegment(sketch, "E203.1.0.0", {"start": v(17.78, 42.06) * mm, "end": v(17.78, 45.34) * mm});
            skLineSegment(sketch, "E203.1.0.1", {"start": v(12.7, 45.34) * mm, "end": v(17.78, 45.34) * mm});
            skLineSegment(sketch, "E203.1.0.2", {"start": v(12.7, 42.06) * mm, "end": v(17.78, 42.06) * mm});
            skLineSegment(sketch, "E203.1.0.3", {"start": v(12.7, 42.06) * mm, "end": v(12.7, 45.34) * mm});
            skLineSegment(sketch, "E203.2.0.0", {"start": v(27.94, 42.06) * mm, "end": v(27.94, 45.34) * mm});
            skLineSegment(sketch, "E203.2.0.1", {"start": v(22.86, 45.34) * mm, "end": v(27.94, 45.34) * mm});
            skLineSegment(sketch, "E203.2.0.2", {"start": v(22.86, 42.06) * mm, "end": v(27.94, 42.06) * mm});
            skLineSegment(sketch, "E203.2.0.3", {"start": v(22.86, 42.06) * mm, "end": v(22.86, 45.34) * mm});
            skLineSegment(sketch, "E203.3.0.0", {"start": v(38.1, 42.06) * mm, "end": v(38.1, 45.34) * mm});
            skLineSegment(sketch, "E203.3.0.1", {"start": v(33.02, 45.34) * mm, "end": v(38.1, 45.34) * mm});
            skLineSegment(sketch, "E203.3.0.2", {"start": v(33.02, 42.06) * mm, "end": v(38.1, 42.06) * mm});
            skLineSegment(sketch, "E203.3.0.3", {"start": v(33.02, 42.06) * mm, "end": v(33.02, 45.34) * mm});
            skLineSegment(sketch, "E203.4.0.0", {"start": v(48.26, 42.06) * mm, "end": v(48.26, 45.34) * mm});
            skLineSegment(sketch, "E203.4.0.1", {"start": v(43.18, 45.34) * mm, "end": v(48.26, 45.34) * mm});
            skLineSegment(sketch, "E203.4.0.2", {"start": v(43.18, 42.06) * mm, "end": v(48.26, 42.06) * mm});
            skLineSegment(sketch, "E203.4.0.3", {"start": v(43.18, 42.06) * mm, "end": v(43.18, 45.34) * mm});
            skLineSegment(sketch, "E203.5.0.0", {"start": v(58.42, 42.06) * mm, "end": v(58.42, 45.34) * mm});
            skLineSegment(sketch, "E203.5.0.1", {"start": v(53.34, 45.34) * mm, "end": v(58.42, 45.34) * mm});
            skLineSegment(sketch, "E203.5.0.2", {"start": v(53.34, 42.06) * mm, "end": v(58.42, 42.06) * mm});
            skLineSegment(sketch, "E203.5.0.3", {"start": v(53.34, 42.06) * mm, "end": v(53.34, 45.34) * mm});
            skLineSegment(sketch, "E203.6.0.0", {"start": v(68.58, 42.06) * mm, "end": v(68.58, 45.34) * mm});
            skLineSegment(sketch, "E203.6.0.1", {"start": v(63.5, 45.34) * mm, "end": v(68.58, 45.34) * mm});
            skLineSegment(sketch, "E203.6.0.2", {"start": v(63.5, 42.06) * mm, "end": v(68.58, 42.06) * mm});
            skLineSegment(sketch, "E203.6.0.3", {"start": v(63.5, 42.06) * mm, "end": v(63.5, 45.34) * mm});
            skLineSegment(sketch, "E203.7.0.0", {"start": v(78.74, 42.06) * mm, "end": v(78.74, 45.34) * mm});
            skLineSegment(sketch, "E203.7.0.1", {"start": v(73.66, 45.34) * mm, "end": v(78.74, 45.34) * mm});
            skLineSegment(sketch, "E203.7.0.2", {"start": v(73.66, 42.06) * mm, "end": v(78.74, 42.06) * mm});
            skLineSegment(sketch, "E203.7.0.3", {"start": v(73.66, 42.06) * mm, "end": v(73.66, 45.34) * mm});
            skLineSegment(sketch, "E203.8.0.0", {"start": v(88.9, 42.06) * mm, "end": v(88.9, 45.34) * mm});
            skLineSegment(sketch, "E203.8.0.1", {"start": v(83.82, 45.34) * mm, "end": v(88.9, 45.34) * mm});
            skLineSegment(sketch, "E203.8.0.2", {"start": v(83.82, 42.06) * mm, "end": v(88.9, 42.06) * mm});
            skLineSegment(sketch, "E203.8.0.3", {"start": v(83.82, 42.06) * mm, "end": v(83.82, 45.34) * mm});
            skLineSegment(sketch, "E203.9.0.0", {"start": v(99.06, 42.06) * mm, "end": v(99.06, 45.34) * mm});
            skLineSegment(sketch, "E203.9.0.1", {"start": v(93.98, 45.34) * mm, "end": v(99.06, 45.34) * mm});
            skLineSegment(sketch, "E203.9.0.2", {"start": v(93.98, 42.06) * mm, "end": v(99.06, 42.06) * mm});
            skLineSegment(sketch, "E203.9.0.3", {"start": v(93.98, 42.06) * mm, "end": v(93.98, 45.34) * mm});
            skLineSegment(sketch, "E203.10.0.0", {"start": v(109.22, 42.06) * mm, "end": v(109.22, 45.34) * mm});
            skLineSegment(sketch, "E203.10.0.1", {"start": v(104.14, 45.34) * mm, "end": v(109.22, 45.34) * mm});
            skLineSegment(sketch, "E203.10.0.2", {"start": v(104.14, 42.06) * mm, "end": v(109.22, 42.06) * mm});
            skLineSegment(sketch, "E203.10.0.3", {"start": v(104.14, 42.06) * mm, "end": v(104.14, 45.34) * mm});
            skLineSegment(sketch, "E203.11.0.0", {"start": v(119.38, 42.06) * mm, "end": v(119.38, 45.34) * mm});
            skLineSegment(sketch, "E203.11.0.1", {"start": v(114.3, 45.34) * mm, "end": v(119.38, 45.34) * mm});
            skLineSegment(sketch, "E203.11.0.2", {"start": v(114.3, 42.06) * mm, "end": v(119.38, 42.06) * mm});
            skLineSegment(sketch, "E203.11.0.3", {"start": v(114.3, 42.06) * mm, "end": v(114.3, 45.34) * mm});
            skLineSegment(sketch, "E203.12.0.0", {"start": v(129.54, 42.06) * mm, "end": v(129.54, 45.34) * mm});
            skLineSegment(sketch, "E203.12.0.1", {"start": v(124.46, 45.34) * mm, "end": v(129.54, 45.34) * mm});
            skLineSegment(sketch, "E203.12.0.2", {"start": v(124.46, 42.06) * mm, "end": v(129.54, 42.06) * mm});
            skLineSegment(sketch, "E203.12.0.3", {"start": v(124.46, 42.06) * mm, "end": v(124.46, 45.34) * mm});
            skLineSegment(sketch, "E203.13.0.0", {"start": v(139.7, 42.06) * mm, "end": v(139.7, 45.34) * mm});
            skLineSegment(sketch, "E203.13.0.1", {"start": v(134.62, 45.34) * mm, "end": v(139.7, 45.34) * mm});
            skLineSegment(sketch, "E203.13.0.2", {"start": v(134.62, 42.06) * mm, "end": v(139.7, 42.06) * mm});
            skLineSegment(sketch, "E203.13.0.3", {"start": v(134.62, 42.06) * mm, "end": v(134.62, 45.34) * mm});
            skLineSegment(sketch, "E203.direction1", {"start": v(2.54, 42.06) * mm, "end": v(12.7, 42.06) * mm, "construction": true});
            skLineSegment(sketch, "E204.MirrorCS", {"start": v(-2.54, 42.06) * mm, "end": v(-2.54, 45.34) * mm});
            skLineSegment(sketch, "E205.MirrorCS", {"start": v(-83.82, 42.06) * mm, "end": v(-83.82, 45.34) * mm});
            skLineSegment(sketch, "E206.MirrorCS", {"start": v(-104.14, 42.06) * mm, "end": v(-104.14, 45.34) * mm});
            skLineSegment(sketch, "E207.MirrorCS", {"start": v(-33.02, 42.06) * mm, "end": v(-33.02, 45.34) * mm});
            skLineSegment(sketch, "E208.MirrorCS", {"start": v(-7.62, 42.06) * mm, "end": v(-7.62, 45.34) * mm});
            skLineSegment(sketch, "E209.MirrorCS", {"start": v(-99.06, 42.06) * mm, "end": v(-99.06, 45.34) * mm});
            skLineSegment(sketch, "E210.MirrorCS", {"start": v(-53.34, 42.06) * mm, "end": v(-53.34, 45.34) * mm});
            skLineSegment(sketch, "E211.MirrorCS", {"start": v(-139.7, 42.06) * mm, "end": v(-139.7, 45.34) * mm});
            skLineSegment(sketch, "E212.MirrorCS", {"start": v(-119.38, 42.06) * mm, "end": v(-119.38, 45.34) * mm});
            skLineSegment(sketch, "E213.MirrorCS", {"start": v(-134.62, 42.06) * mm, "end": v(-134.62, 45.34) * mm});
            skLineSegment(sketch, "E214.MirrorCS", {"start": v(-68.58, 42.06) * mm, "end": v(-68.58, 45.34) * mm});
            skLineSegment(sketch, "E215.MirrorCS", {"start": v(-73.66, 42.06) * mm, "end": v(-73.66, 45.34) * mm});
            skLineSegment(sketch, "E216.MirrorCS", {"start": v(-38.1, 42.06) * mm, "end": v(-38.1, 45.34) * mm});
            skLineSegment(sketch, "E217.MirrorCS", {"start": v(-124.46, 42.06) * mm, "end": v(-124.46, 45.34) * mm});
            skLineSegment(sketch, "E218.MirrorCS", {"start": v(-58.42, 42.06) * mm, "end": v(-58.42, 45.34) * mm});
            skLineSegment(sketch, "E219.MirrorCS", {"start": v(-109.22, 42.06) * mm, "end": v(-109.22, 45.34) * mm});
            skLineSegment(sketch, "E220.MirrorCS", {"start": v(-63.5, 42.06) * mm, "end": v(-63.5, 45.34) * mm});
            skLineSegment(sketch, "E221.MirrorCS", {"start": v(-12.7, 42.06) * mm, "end": v(-12.7, 45.34) * mm});
            skLineSegment(sketch, "E222.MirrorCS", {"start": v(-43.18, 42.06) * mm, "end": v(-43.18, 45.34) * mm});
            skLineSegment(sketch, "E223.MirrorCS", {"start": v(-129.54, 42.06) * mm, "end": v(-129.54, 45.34) * mm});
            skLineSegment(sketch, "E224.MirrorCS", {"start": v(-17.78, 42.06) * mm, "end": v(-17.78, 45.34) * mm});
            skLineSegment(sketch, "E225.MirrorCS", {"start": v(-48.26, 42.06) * mm, "end": v(-48.26, 45.34) * mm});
            skLineSegment(sketch, "E226.MirrorCS", {"start": v(-93.98, 42.06) * mm, "end": v(-93.98, 45.34) * mm});
            skLineSegment(sketch, "E227.MirrorCS", {"start": v(-27.94, 42.06) * mm, "end": v(-27.94, 45.34) * mm});
            skLineSegment(sketch, "E228.MirrorCS", {"start": v(-22.86, 42.06) * mm, "end": v(-22.86, 45.34) * mm});
            skLineSegment(sketch, "E229.MirrorCS", {"start": v(-88.9, 42.06) * mm, "end": v(-88.9, 45.34) * mm});
            skLineSegment(sketch, "E230.MirrorCS", {"start": v(-114.3, 42.06) * mm, "end": v(-114.3, 45.34) * mm});
            skLineSegment(sketch, "E231.MirrorCS", {"start": v(-78.74, 42.06) * mm, "end": v(-78.74, 45.34) * mm});
            skLineSegment(sketch, "E232.MirrorCS", {"start": v(-2.54, 42.06) * mm, "end": v(-7.62, 42.06) * mm});
            skLineSegment(sketch, "E233.MirrorCS", {"start": v(-2.54, 45.34) * mm, "end": v(-7.62, 45.34) * mm});
            skLineSegment(sketch, "E234.MirrorCS", {"start": v(-63.5, 45.34) * mm, "end": v(-68.58, 45.34) * mm});
            skLineSegment(sketch, "E235.MirrorCS", {"start": v(-43.18, 42.06) * mm, "end": v(-48.26, 42.06) * mm});
            skLineSegment(sketch, "E236.MirrorCS", {"start": v(-124.46, 45.34) * mm, "end": v(-129.54, 45.34) * mm});
            skLineSegment(sketch, "E237.MirrorCS", {"start": v(-114.3, 42.06) * mm, "end": v(-119.38, 42.06) * mm});
            skLineSegment(sketch, "E238.MirrorCS", {"start": v(-22.86, 42.06) * mm, "end": v(-27.94, 42.06) * mm});
            skLineSegment(sketch, "E239.MirrorCS", {"start": v(-53.34, 42.06) * mm, "end": v(-58.42, 42.06) * mm});
            skLineSegment(sketch, "E240.MirrorCS", {"start": v(-12.7, 45.34) * mm, "end": v(-17.78, 45.34) * mm});
            skLineSegment(sketch, "E241.MirrorCS", {"start": v(-33.02, 45.34) * mm, "end": v(-38.1, 45.34) * mm});
            skLineSegment(sketch, "E242.MirrorCS", {"start": v(-104.14, 45.34) * mm, "end": v(-109.22, 45.34) * mm});
            skLineSegment(sketch, "E243.MirrorCS", {"start": v(-43.18, 45.34) * mm, "end": v(-48.26, 45.34) * mm});
            skLineSegment(sketch, "E244.MirrorCS", {"start": v(-124.46, 42.06) * mm, "end": v(-129.54, 42.06) * mm});
            skLineSegment(sketch, "E245.MirrorCS", {"start": v(-53.34, 45.34) * mm, "end": v(-58.42, 45.34) * mm});
            skLineSegment(sketch, "E246.MirrorCS", {"start": v(-73.66, 45.34) * mm, "end": v(-78.74, 45.34) * mm});
            skLineSegment(sketch, "E247.MirrorCS", {"start": v(-83.82, 42.06) * mm, "end": v(-88.9, 42.06) * mm});
            skLineSegment(sketch, "E248.MirrorCS", {"start": v(-63.5, 42.06) * mm, "end": v(-68.58, 42.06) * mm});
            skLineSegment(sketch, "E249.MirrorCS", {"start": v(-83.82, 45.34) * mm, "end": v(-88.9, 45.34) * mm});
            skLineSegment(sketch, "E250.MirrorCS", {"start": v(-114.3, 45.34) * mm, "end": v(-119.38, 45.34) * mm});
            skLineSegment(sketch, "E251.MirrorCS", {"start": v(-22.86, 45.34) * mm, "end": v(-27.94, 45.34) * mm});
            skLineSegment(sketch, "E252.MirrorCS", {"start": v(-12.7, 42.06) * mm, "end": v(-17.78, 42.06) * mm});
            skLineSegment(sketch, "E253.MirrorCS", {"start": v(-93.98, 42.06) * mm, "end": v(-99.06, 42.06) * mm});
            skLineSegment(sketch, "E254.MirrorCS", {"start": v(-134.62, 45.34) * mm, "end": v(-139.7, 45.34) * mm});
            skLineSegment(sketch, "E255.MirrorCS", {"start": v(-93.98, 45.34) * mm, "end": v(-99.06, 45.34) * mm});
            skLineSegment(sketch, "E256.MirrorCS", {"start": v(-33.02, 42.06) * mm, "end": v(-38.1, 42.06) * mm});
            skLineSegment(sketch, "E257.MirrorCS", {"start": v(-73.66, 42.06) * mm, "end": v(-78.74, 42.06) * mm});
            skLineSegment(sketch, "E258.MirrorCS", {"start": v(-104.14, 42.06) * mm, "end": v(-109.22, 42.06) * mm});
            skLineSegment(sketch, "E259.MirrorCS", {"start": v(-134.62, 42.06) * mm, "end": v(-139.7, 42.06) * mm});
            skSolve(sketch);
        }
        {
            var Q0;
            Q0 = qSketchRegion(id + "F11", true);
            var Q1;
            Q1=makeQuery(id+"F10.opExtrude","SWEPT_FACE",FACE,{"disambiguationData":[OSD([sQuery(id+"F9.wireOp",EDGE,"E199.2")])]});
            extrude(context, id + "F12", {"entities" : qUnion([Q0]), "operationType" : NewBodyOperationType.REMOVE, "endBound" : BoundingType.UP_TO_SURFACE, "oppositeDirection" : true, "endBoundEntityFace" : qUnion([Q1]), "depth" : 25.4 * mm});
        }
        {
            var Q0;
            Q0=qCreatedBy(makeId("Right.planeOp"),FACE);
            var sketch = newSketch(context, id + "F13", { "sketchPlane" : qUnion([Q0])});
            skLineSegment(sketch, "E260.0.0", {"start": v(-61.11, -2.6) * mm, "end": v(61.11, -2.6) * mm});
            skLineSegment(sketch, "E260.0.1", {"start": v(61.11, -2.6) * mm, "end": v(61.11, 2.6) * mm});
            skLineSegment(sketch, "E260.0.2", {"start": v(61.11, 2.6) * mm, "end": v(55.91, 2.6) * mm});
            skLineSegment(sketch, "E260.0.3", {"start": v(55.91, 2.6) * mm, "end": v(-61.11, 2.6) * mm});
            skLineSegment(sketch, "E260.0.4", {"start": v(-61.11, 2.6) * mm, "end": v(-61.11, -2.6) * mm});
            skSolve(sketch);
        }
        {
            var Q0;
            Q0 = qSketchRegion(id + "F13", true);
            extrude(context, id + "F14", {"entities" : qUnion([Q0]), "depth" : 142.24 * mm, "hasSecondDirection" : true, "secondDirectionOppositeDirection" : true, "secondDirectionDepth" : 142.24 * mm});
        }
        {
            var Q0;
            Q0=makeQuery(id+"F2.opExtrude","CAP_FACE",FACE,{"disambiguationData":[OSD([sQuery(id+"F1.wireOp",EDGE,"E12.0"),sQuery(id+"F1.wireOp",EDGE,"E12.1"),sQuery(id+"F1.wireOp",EDGE,"E12.2"),sQuery(id+"F1.wireOp",EDGE,"E12.3")])],"isStart":false});
            var sketch = newSketch(context, id + "F15", { "sketchPlane" : qUnion([Q0])});
            skPoint(sketch, "E261.0", {"position": v(-61.11, -2.6) * mm});
            skPoint(sketch, "E262.0", {"position": v(-66.31, 16.45) * mm});
            skLineSegment(sketch, "E263", {"start": v(-66.31, 16.45) * mm, "end": v(-59.13, 22.27) * mm});
            skLineSegment(sketch, "E264", {"start": v(-59.13, 22.27) * mm, "end": v(-55.86, 18.23) * mm});
            skLineSegment(sketch, "E265", {"start": v(-55.86, 18.23) * mm, "end": v(-51.81, 21.51) * mm});
            skLineSegment(sketch, "E266", {"start": v(-51.81, 21.51) * mm, "end": v(-55.09, 25.55) * mm});
            skLineSegment(sketch, "E267", {"start": v(-55.09, 25.55) * mm, "end": v(-51.04, 28.83) * mm});
            skLineSegment(sketch, "E268", {"start": v(-51.04, 28.83) * mm, "end": v(-47.77, 24.79) * mm});
            skPoint(sketch, "E269", {"position": v(-47.77, 24.79) * mm});
            skLineSegment(sketch, "E270.1.0.0", {"start": v(-42.96, 35.38) * mm, "end": v(-39.68, 31.34) * mm});
            skLineSegment(sketch, "E270.1.0.1", {"start": v(-47, 32.1) * mm, "end": v(-42.96, 35.38) * mm});
            skLineSegment(sketch, "E270.1.0.2", {"start": v(-43.73, 28.06) * mm, "end": v(-47, 32.1) * mm});
            skLineSegment(sketch, "E270.1.0.3", {"start": v(-47.77, 24.78) * mm, "end": v(-43.73, 28.06) * mm});
            skLineSegment(sketch, "E270.2.0.0", {"start": v(-34.87, 41.93) * mm, "end": v(-31.6, 37.9) * mm});
            skLineSegment(sketch, "E270.2.0.1", {"start": v(-38.92, 38.66) * mm, "end": v(-34.87, 41.93) * mm});
            skLineSegment(sketch, "E270.2.0.2", {"start": v(-35.64, 34.62) * mm, "end": v(-38.92, 38.66) * mm});
            skLineSegment(sketch, "E270.2.0.3", {"start": v(-39.69, 31.34) * mm, "end": v(-35.64, 34.62) * mm});
            skLineSegment(sketch, "E270.3.0.0", {"start": v(-26.79, 48.49) * mm, "end": v(-23.51, 44.45) * mm});
            skLineSegment(sketch, "E270.3.0.1", {"start": v(-30.83, 45.2) * mm, "end": v(-26.79, 48.49) * mm});
            skLineSegment(sketch, "E270.3.0.2", {"start": v(-27.56, 41.17) * mm, "end": v(-30.83, 45.2) * mm});
            skLineSegment(sketch, "E270.3.0.3", {"start": v(-31.6, 37.9) * mm, "end": v(-27.56, 41.17) * mm});
            skLineSegment(sketch, "E270.4.0.0", {"start": v(-18.7, 55.04) * mm, "end": v(-15.43, 51) * mm});
            skLineSegment(sketch, "E270.4.0.1", {"start": v(-22.75, 51.76) * mm, "end": v(-18.7, 55.04) * mm});
            skLineSegment(sketch, "E270.4.0.2", {"start": v(-19.47, 47.72) * mm, "end": v(-22.75, 51.76) * mm});
            skLineSegment(sketch, "E270.4.0.3", {"start": v(-23.52, 44.44) * mm, "end": v(-19.47, 47.72) * mm});
            skLineSegment(sketch, "E270.5.0.0", {"start": v(-10.62, 61.6) * mm, "end": v(-7.34, 57.55) * mm});
            skLineSegment(sketch, "E270.5.0.1", {"start": v(-14.66, 58.32) * mm, "end": v(-10.62, 61.6) * mm});
            skLineSegment(sketch, "E270.5.0.2", {"start": v(-11.39, 54.28) * mm, "end": v(-14.66, 58.32) * mm});
            skLineSegment(sketch, "E270.5.0.3", {"start": v(-15.43, 51) * mm, "end": v(-11.39, 54.28) * mm});
            skLineSegment(sketch, "E270.6.0.0", {"start": v(-2.53, 68.15) * mm, "end": v(0.74, 64.1) * mm});
            skLineSegment(sketch, "E270.6.0.1", {"start": v(-6.58, 64.87) * mm, "end": v(-2.53, 68.15) * mm});
            skLineSegment(sketch, "E270.6.0.2", {"start": v(-3.3, 60.83) * mm, "end": v(-6.58, 64.87) * mm});
            skLineSegment(sketch, "E270.6.0.3", {"start": v(-7.35, 57.55) * mm, "end": v(-3.3, 60.83) * mm});
            skLineSegment(sketch, "E270.7.0.0", {"start": v(5.55, 74.7) * mm, "end": v(8.83, 70.66) * mm});
            skLineSegment(sketch, "E270.7.0.1", {"start": v(1.5, 71.42) * mm, "end": v(5.55, 74.7) * mm});
            skLineSegment(sketch, "E270.7.0.2", {"start": v(4.78, 67.38) * mm, "end": v(1.5, 71.42) * mm});
            skLineSegment(sketch, "E270.7.0.3", {"start": v(0.74, 64.1) * mm, "end": v(4.78, 67.38) * mm});
            skLineSegment(sketch, "E270.8.0.0", {"start": v(13.64, 81.25) * mm, "end": v(16.91, 77.21) * mm});
            skLineSegment(sketch, "E270.8.0.1", {"start": v(9.6, 77.97) * mm, "end": v(13.64, 81.25) * mm});
            skLineSegment(sketch, "E270.8.0.2", {"start": v(12.86, 73.93) * mm, "end": v(9.6, 77.97) * mm});
            skLineSegment(sketch, "E270.8.0.3", {"start": v(8.82, 70.66) * mm, "end": v(12.86, 73.93) * mm});
            skLineSegment(sketch, "E270.9.0.0", {"start": v(21.72, 87.8) * mm, "end": v(25, 83.77) * mm});
            skLineSegment(sketch, "E270.9.0.1", {"start": v(17.68, 84.53) * mm, "end": v(21.72, 87.8) * mm});
            skLineSegment(sketch, "E270.9.0.2", {"start": v(20.95, 80.49) * mm, "end": v(17.68, 84.53) * mm});
            skLineSegment(sketch, "E270.9.0.3", {"start": v(16.9, 77.2) * mm, "end": v(20.95, 80.49) * mm});
            skLineSegment(sketch, "E270.10.0.0", {"start": v(29.8, 94.36) * mm, "end": v(33.08, 90.32) * mm});
            skLineSegment(sketch, "E270.10.0.1", {"start": v(25.76, 91.08) * mm, "end": v(29.8, 94.36) * mm});
            skLineSegment(sketch, "E270.10.0.2", {"start": v(29.03, 87.04) * mm, "end": v(25.76, 91.08) * mm});
            skLineSegment(sketch, "E270.10.0.3", {"start": v(24.99, 83.76) * mm, "end": v(29.03, 87.04) * mm});
            skLineSegment(sketch, "E270.11.0.2", {"start": v(37.12, 93.6) * mm, "end": v(33.84, 97.63) * mm});
            skLineSegment(sketch, "E270.11.0.3", {"start": v(33.07, 90.31) * mm, "end": v(37.12, 93.6) * mm});
            skLineSegment(sketch, "E270.direction1", {"start": v(-55.86, 18.23) * mm, "end": v(-47.77, 24.78) * mm, "construction": true});
            skPoint(sketch, "E271.0", {"position": v(42.06, 104.3) * mm});
            skLineSegment(sketch, "E272", {"start": v(33.84, 97.63) * mm, "end": v(42.06, 104.3) * mm});
            skLineSegment(sketch, "E273", {"start": v(42.06, 104.3) * mm, "end": v(47.27, 104.3) * mm});
            skLineSegment(sketch, "E274", {"start": v(47.27, 104.3) * mm, "end": v(47.27, 99.1) * mm});
            skLineSegment(sketch, "E275", {"start": v(47.27, 99.1) * mm, "end": v(55.9, 99.1) * mm});
            skLineSegment(sketch, "E276", {"start": v(55.9, 99.1) * mm, "end": v(55.9, 104.3) * mm});
            skLineSegment(sketch, "E277", {"start": v(55.9, 104.3) * mm, "end": v(61.11, 104.3) * mm});
            skLineSegment(sketch, "E278", {"start": v(61.11, 104.3) * mm, "end": v(61.11, -2.6) * mm});
            skPoint(sketch, "E279.0", {"position": v(61.11, -2.6) * mm});
            skLineSegment(sketch, "E280", {"start": v(61.11, -2.6) * mm, "end": v(55.9, -2.6) * mm});
            skLineSegment(sketch, "E281", {"start": v(55.9, -2.6) * mm, "end": v(55.9, 2.6) * mm});
            skLineSegment(sketch, "E282", {"start": v(55.9, 2.6) * mm, "end": v(50.7, 2.6) * mm});
            skLineSegment(sketch, "E283", {"start": v(50.7, 2.6) * mm, "end": v(50.7, -2.6) * mm});
            skLineSegment(sketch, "E284.1.0.0", {"start": v(50.7, -2.6) * mm, "end": v(45.5, -2.6) * mm});
            skLineSegment(sketch, "E284.1.0.1", {"start": v(45.5, -2.6) * mm, "end": v(45.5, 2.6) * mm});
            skLineSegment(sketch, "E284.1.0.2", {"start": v(45.5, 2.6) * mm, "end": v(40.29, 2.6) * mm});
            skLineSegment(sketch, "E284.1.0.3", {"start": v(40.29, 2.6) * mm, "end": v(40.29, -2.6) * mm});
            skLineSegment(sketch, "E284.2.0.0", {"start": v(40.29, -2.6) * mm, "end": v(35.08, -2.6) * mm});
            skLineSegment(sketch, "E284.2.0.1", {"start": v(35.08, -2.6) * mm, "end": v(35.08, 2.6) * mm});
            skLineSegment(sketch, "E284.2.0.2", {"start": v(35.08, 2.6) * mm, "end": v(29.87, 2.6) * mm});
            skLineSegment(sketch, "E284.2.0.3", {"start": v(29.87, 2.6) * mm, "end": v(29.87, -2.6) * mm});
            skLineSegment(sketch, "E284.3.0.0", {"start": v(29.87, -2.6) * mm, "end": v(24.67, -2.6) * mm});
            skLineSegment(sketch, "E284.3.0.1", {"start": v(24.67, -2.6) * mm, "end": v(24.67, 2.6) * mm});
            skLineSegment(sketch, "E284.3.0.2", {"start": v(24.67, 2.6) * mm, "end": v(19.46, 2.6) * mm});
            skLineSegment(sketch, "E284.3.0.3", {"start": v(19.46, 2.6) * mm, "end": v(19.46, -2.6) * mm});
            skLineSegment(sketch, "E284.4.0.0", {"start": v(19.46, -2.6) * mm, "end": v(14.25, -2.6) * mm});
            skLineSegment(sketch, "E284.4.0.1", {"start": v(14.25, -2.6) * mm, "end": v(14.25, 2.6) * mm});
            skLineSegment(sketch, "E284.4.0.2", {"start": v(14.25, 2.6) * mm, "end": v(9.04, 2.6) * mm});
            skLineSegment(sketch, "E284.4.0.3", {"start": v(9.04, 2.6) * mm, "end": v(9.04, -2.6) * mm});
            skLineSegment(sketch, "E284.5.0.0", {"start": v(9.04, -2.6) * mm, "end": v(3.84, -2.6) * mm});
            skLineSegment(sketch, "E284.5.0.1", {"start": v(3.84, -2.6) * mm, "end": v(3.84, 2.6) * mm});
            skLineSegment(sketch, "E284.5.0.2", {"start": v(3.84, 2.6) * mm, "end": v(-1.37, 2.6) * mm});
            skLineSegment(sketch, "E284.5.0.3", {"start": v(-1.37, 2.6) * mm, "end": v(-1.37, -2.6) * mm});
            skLineSegment(sketch, "E284.6.0.0", {"start": v(-1.37, -2.6) * mm, "end": v(-6.58, -2.6) * mm});
            skLineSegment(sketch, "E284.6.0.1", {"start": v(-6.58, -2.6) * mm, "end": v(-6.58, 2.6) * mm});
            skLineSegment(sketch, "E284.6.0.2", {"start": v(-6.58, 2.6) * mm, "end": v(-11.78, 2.6) * mm});
            skLineSegment(sketch, "E284.6.0.3", {"start": v(-11.78, 2.6) * mm, "end": v(-11.78, -2.6) * mm});
            skLineSegment(sketch, "E284.7.0.0", {"start": v(-11.78, -2.6) * mm, "end": v(-17, -2.6) * mm});
            skLineSegment(sketch, "E284.7.0.1", {"start": v(-17, -2.6) * mm, "end": v(-17, 2.6) * mm});
            skLineSegment(sketch, "E284.7.0.2", {"start": v(-17, 2.6) * mm, "end": v(-22.2, 2.6) * mm});
            skLineSegment(sketch, "E284.7.0.3", {"start": v(-22.2, 2.6) * mm, "end": v(-22.2, -2.6) * mm});
            skLineSegment(sketch, "E284.8.0.0", {"start": v(-22.2, -2.6) * mm, "end": v(-27.4, -2.6) * mm});
            skLineSegment(sketch, "E284.8.0.1", {"start": v(-27.4, -2.6) * mm, "end": v(-27.4, 2.6) * mm});
            skLineSegment(sketch, "E284.8.0.2", {"start": v(-27.4, 2.6) * mm, "end": v(-32.61, 2.6) * mm});
            skLineSegment(sketch, "E284.8.0.3", {"start": v(-32.61, 2.6) * mm, "end": v(-32.61, -2.6) * mm});
            skLineSegment(sketch, "E284.9.0.0", {"start": v(-32.61, -2.6) * mm, "end": v(-37.82, -2.6) * mm});
            skLineSegment(sketch, "E284.9.0.1", {"start": v(-37.82, -2.6) * mm, "end": v(-37.82, 2.6) * mm});
            skLineSegment(sketch, "E284.9.0.2", {"start": v(-37.82, 2.6) * mm, "end": v(-43.03, 2.6) * mm});
            skLineSegment(sketch, "E284.9.0.3", {"start": v(-43.03, 2.6) * mm, "end": v(-43.03, -2.6) * mm});
            skLineSegment(sketch, "E284.10.0.0", {"start": v(-43.03, -2.6) * mm, "end": v(-48.23, -2.6) * mm});
            skLineSegment(sketch, "E284.10.0.1", {"start": v(-48.23, -2.6) * mm, "end": v(-48.23, 2.6) * mm});
            skLineSegment(sketch, "E284.10.0.2", {"start": v(-48.23, 2.6) * mm, "end": v(-53.44, 2.6) * mm});
            skLineSegment(sketch, "E284.10.0.3", {"start": v(-53.44, 2.6) * mm, "end": v(-53.44, -2.6) * mm});
            skLineSegment(sketch, "E284.direction1", {"start": v(50.7, -2.6) * mm, "end": v(40.29, -2.6) * mm, "construction": true});
            skLineSegment(sketch, "E285", {"start": v(-66.31, 16.45) * mm, "end": v(-66.31, 12.46) * mm});
            skLineSegment(sketch, "E286", {"start": v(-66.31, 12.46) * mm, "end": v(-61.11, 12.46) * mm});
            skLineSegment(sketch, "E287", {"start": v(-61.11, 12.46) * mm, "end": v(-61.11, -2.6) * mm});
            skLineSegment(sketch, "E288", {"start": v(-53.44, -2.6) * mm, "end": v(-61.11, -2.6) * mm});
            skSolve(sketch);
        }
        {
            var Q0;
            Q0 = qSketchRegion(id + "F15", true);
            extrude(context, id + "F16", {"entities" : qUnion([Q0]), "oppositeDirection" : true, "depth" : 5.2 * mm});
        }
        {
            var Q0;
            Q0=makeQuery(id+"F10.opExtrude","SWEPT_FACE",FACE,{"disambiguationData":[OSD([sQuery(id+"F9.wireOp",EDGE,"E199.0")])]});
            var sketch = newSketch(context, id + "F17", { "sketchPlane" : qUnion([Q0])});
            skLineSegment(sketch, "E289.0", {"start": v(137.03, 55.9) * mm, "end": v(137.03, 61.11) * mm});
            skLineSegment(sketch, "E289.1", {"start": v(137.03, 55.9) * mm, "end": v(142.24, 55.9) * mm});
            skLineSegment(sketch, "E289.2", {"start": v(137.03, 47.27) * mm, "end": v(142.24, 47.27) * mm});
            skLineSegment(sketch, "E289.3", {"start": v(137.03, 42.06) * mm, "end": v(137.03, 47.27) * mm});
            skLineSegment(sketch, "E289.4", {"start": v(142.24, 42.06) * mm, "end": v(142.24, 47.27) * mm});
            skLineSegment(sketch, "E289.5", {"start": v(142.24, 61.11) * mm, "end": v(137.03, 61.11) * mm});
            skPoint(sketch, "E290.orphan", {"position": v(-142.24, 61.11) * mm});
            skLineSegment(sketch, "E291.trimOffspring", {"start": v(142.24, 55.9) * mm, "end": v(142.24, 61.11) * mm});
            skLineSegment(sketch, "E292", {"start": v(137.03, 42.06) * mm, "end": v(142.24, 42.06) * mm});
            skLineSegment(sketch, "E293.MirrorCS", {"start": v(-142.24, 55.9) * mm, "end": v(-142.24, 61.11) * mm});
            skLineSegment(sketch, "E294.MirrorCS", {"start": v(-137.03, 55.9) * mm, "end": v(-137.03, 61.11) * mm});
            skLineSegment(sketch, "E295.MirrorCS", {"start": v(-137.03, 47.27) * mm, "end": v(-142.24, 47.27) * mm});
            skLineSegment(sketch, "E296.MirrorCS", {"start": v(-142.24, 42.06) * mm, "end": v(-142.24, 47.27) * mm});
            skLineSegment(sketch, "E297.MirrorCS", {"start": v(-142.24, 61.11) * mm, "end": v(-137.03, 61.11) * mm});
            skLineSegment(sketch, "E298.MirrorCS", {"start": v(-137.03, 42.06) * mm, "end": v(-137.03, 47.27) * mm});
            skLineSegment(sketch, "E299.MirrorCS", {"start": v(-137.03, 42.06) * mm, "end": v(-142.24, 42.06) * mm});
            skLineSegment(sketch, "E300.MirrorCS", {"start": v(-137.03, 55.9) * mm, "end": v(-142.24, 55.9) * mm});
            skSolve(sketch);
        }
        {
            var Q0;
            Q0 = qSketchRegion(id + "F17", true);
            var Q1;
            Q1=makeQuery(id+"F10.opExtrude","SWEPT_FACE",FACE,{"disambiguationData":[OSD([sQuery(id+"F9.wireOp",EDGE,"E199.2")])]});
            extrude(context, id + "F18", {"entities" : qUnion([Q0]), "operationType" : NewBodyOperationType.REMOVE, "endBound" : BoundingType.UP_TO_SURFACE, "oppositeDirection" : true, "endBoundEntityFace" : qUnion([Q1]), "depth" : 25.4 * mm});
        }
        {
            var Q0;
            Q0=makeQuery(id+"F2.opExtrude","SWEPT_FACE",FACE,{"disambiguationData":[OSD([sQuery(id+"F1.wireOp",EDGE,"E12.2")])]});
            var sketch = newSketch(context, id + "F19", { "sketchPlane" : qUnion([Q0])});
            skLineSegment(sketch, "E301.0.0", {"start": v(142.24, 87.77) * mm, "end": v(142.24, 98.35) * mm});
            skLineSegment(sketch, "E301.0.1", {"start": v(142.24, 98.35) * mm, "end": v(137.03, 98.35) * mm});
            skLineSegment(sketch, "E301.0.2", {"start": v(137.03, 98.35) * mm, "end": v(137.03, 87.77) * mm});
            skLineSegment(sketch, "E301.0.3", {"start": v(137.03, 87.77) * mm, "end": v(142.24, 87.77) * mm});
            skLineSegment(sketch, "E301.1.0", {"start": v(142.24, 77.36) * mm, "end": v(142.24, 82.57) * mm});
            skLineSegment(sketch, "E301.1.1", {"start": v(142.24, 82.57) * mm, "end": v(137.03, 82.57) * mm});
            skLineSegment(sketch, "E301.1.2", {"start": v(137.03, 82.57) * mm, "end": v(137.03, 77.36) * mm});
            skLineSegment(sketch, "E301.1.3", {"start": v(137.03, 77.36) * mm, "end": v(142.24, 77.36) * mm});
            skLineSegment(sketch, "E301.2.0", {"start": v(142.24, 66.96) * mm, "end": v(142.24, 72.16) * mm});
            skLineSegment(sketch, "E301.2.1", {"start": v(142.24, 72.16) * mm, "end": v(137.03, 72.16) * mm});
            skLineSegment(sketch, "E301.2.2", {"start": v(137.03, 72.16) * mm, "end": v(137.03, 66.96) * mm});
            skLineSegment(sketch, "E301.2.3", {"start": v(137.03, 66.96) * mm, "end": v(142.24, 66.96) * mm});
            skLineSegment(sketch, "E301.3.0", {"start": v(142.24, 56.55) * mm, "end": v(142.24, 61.76) * mm});
            skLineSegment(sketch, "E301.3.1", {"start": v(142.24, 61.76) * mm, "end": v(137.03, 61.76) * mm});
            skLineSegment(sketch, "E301.3.2", {"start": v(137.03, 61.76) * mm, "end": v(137.03, 56.55) * mm});
            skLineSegment(sketch, "E301.3.3", {"start": v(137.03, 56.55) * mm, "end": v(142.24, 56.55) * mm});
            skLineSegment(sketch, "E301.4.0", {"start": v(142.24, 46.14) * mm, "end": v(142.24, 51.35) * mm});
            skLineSegment(sketch, "E301.4.1", {"start": v(142.24, 51.35) * mm, "end": v(137.03, 51.35) * mm});
            skLineSegment(sketch, "E301.4.2", {"start": v(137.03, 51.35) * mm, "end": v(137.03, 46.14) * mm});
            skLineSegment(sketch, "E301.4.3", {"start": v(137.03, 46.14) * mm, "end": v(142.24, 46.14) * mm});
            skLineSegment(sketch, "E301.5.0", {"start": v(142.24, 35.73) * mm, "end": v(142.24, 40.94) * mm});
            skLineSegment(sketch, "E301.5.1", {"start": v(142.24, 40.94) * mm, "end": v(137.03, 40.94) * mm});
            skLineSegment(sketch, "E301.5.2", {"start": v(137.03, 40.94) * mm, "end": v(137.03, 35.73) * mm});
            skLineSegment(sketch, "E301.5.3", {"start": v(137.03, 35.73) * mm, "end": v(142.24, 35.73) * mm});
            skLineSegment(sketch, "E301.6.0", {"start": v(142.24, 25.33) * mm, "end": v(142.24, 30.53) * mm});
            skLineSegment(sketch, "E301.6.1", {"start": v(142.24, 30.53) * mm, "end": v(137.03, 30.53) * mm});
            skLineSegment(sketch, "E301.6.2", {"start": v(137.03, 30.53) * mm, "end": v(137.03, 25.33) * mm});
            skLineSegment(sketch, "E301.6.3", {"start": v(137.03, 25.33) * mm, "end": v(142.24, 25.33) * mm});
            skLineSegment(sketch, "E301.7.0", {"start": v(142.24, 14.92) * mm, "end": v(142.24, 20.13) * mm});
            skLineSegment(sketch, "E301.7.1", {"start": v(142.24, 20.13) * mm, "end": v(137.03, 20.13) * mm});
            skLineSegment(sketch, "E301.7.2", {"start": v(137.03, 20.13) * mm, "end": v(137.03, 14.92) * mm});
            skLineSegment(sketch, "E301.7.3", {"start": v(137.03, 14.92) * mm, "end": v(142.24, 14.92) * mm});
            skLineSegment(sketch, "E301.8.0", {"start": v(142.24, 4.51) * mm, "end": v(142.24, 9.72) * mm});
            skLineSegment(sketch, "E301.8.1", {"start": v(142.24, 9.72) * mm, "end": v(137.03, 9.72) * mm});
            skLineSegment(sketch, "E301.8.2", {"start": v(137.03, 9.72) * mm, "end": v(137.03, 4.51) * mm});
            skLineSegment(sketch, "E301.8.3", {"start": v(137.03, 4.51) * mm, "end": v(142.24, 4.51) * mm});
            skLineSegment(sketch, "E301.9.0", {"start": v(142.24, -5.9) * mm, "end": v(142.24, -0.69) * mm});
            skLineSegment(sketch, "E301.9.1", {"start": v(142.24, -0.69) * mm, "end": v(137.03, -0.69) * mm});
            skLineSegment(sketch, "E301.9.2", {"start": v(137.03, -0.69) * mm, "end": v(137.03, -5.9) * mm});
            skLineSegment(sketch, "E301.9.3", {"start": v(137.03, -5.9) * mm, "end": v(142.24, -5.9) * mm});
            skLineSegment(sketch, "E301.10.0", {"start": v(142.24, -16.3) * mm, "end": v(142.24, -11.1) * mm});
            skLineSegment(sketch, "E301.10.1", {"start": v(142.24, -11.1) * mm, "end": v(137.03, -11.1) * mm});
            skLineSegment(sketch, "E301.10.2", {"start": v(137.03, -11.1) * mm, "end": v(137.03, -16.3) * mm});
            skLineSegment(sketch, "E301.10.3", {"start": v(137.03, -16.3) * mm, "end": v(142.24, -16.3) * mm});
            skLineSegment(sketch, "E301.11.0", {"start": v(142.24, -26.7) * mm, "end": v(142.24, -21.5) * mm});
            skLineSegment(sketch, "E301.11.1", {"start": v(142.24, -21.5) * mm, "end": v(137.03, -21.5) * mm});
            skLineSegment(sketch, "E301.11.2", {"start": v(137.03, -21.5) * mm, "end": v(137.03, -26.7) * mm});
            skLineSegment(sketch, "E301.11.3", {"start": v(137.03, -26.7) * mm, "end": v(142.24, -26.7) * mm});
            skLineSegment(sketch, "E301.12.0", {"start": v(142.24, -41.16) * mm, "end": v(142.24, -31.91) * mm});
            skLineSegment(sketch, "E301.12.1", {"start": v(142.24, -31.91) * mm, "end": v(137.03, -31.91) * mm});
            skLineSegment(sketch, "E301.12.2", {"start": v(137.03, -31.91) * mm, "end": v(137.03, -41.16) * mm});
            skLineSegment(sketch, "E301.12.3", {"start": v(137.03, -41.16) * mm, "end": v(142.24, -41.16) * mm});
            skLineSegment(sketch, "E302.MirrorCS", {"start": v(-137.03, 14.92) * mm, "end": v(-142.24, 14.92) * mm});
            skLineSegment(sketch, "E303.MirrorCS", {"start": v(-142.24, 82.57) * mm, "end": v(-137.03, 82.57) * mm});
            skLineSegment(sketch, "E304.MirrorCS", {"start": v(-137.03, 9.72) * mm, "end": v(-137.03, 4.51) * mm});
            skLineSegment(sketch, "E305.MirrorCS", {"start": v(-137.03, 20.13) * mm, "end": v(-137.03, 14.92) * mm});
            skLineSegment(sketch, "E306.MirrorCS", {"start": v(-137.03, 51.35) * mm, "end": v(-137.03, 46.14) * mm});
            skLineSegment(sketch, "E307.MirrorCS", {"start": v(-142.24, -0.69) * mm, "end": v(-137.03, -0.69) * mm});
            skLineSegment(sketch, "E308.MirrorCS", {"start": v(-142.24, -26.7) * mm, "end": v(-142.24, -21.5) * mm});
            skLineSegment(sketch, "E309.MirrorCS", {"start": v(-142.24, 9.72) * mm, "end": v(-137.03, 9.72) * mm});
            skLineSegment(sketch, "E310.MirrorCS", {"start": v(-137.03, 25.33) * mm, "end": v(-142.24, 25.33) * mm});
            skLineSegment(sketch, "E311.MirrorCS", {"start": v(-137.03, 66.96) * mm, "end": v(-142.24, 66.96) * mm});
            skLineSegment(sketch, "E312.MirrorCS", {"start": v(-142.24, 72.16) * mm, "end": v(-137.03, 72.16) * mm});
            skLineSegment(sketch, "E313.MirrorCS", {"start": v(-137.03, 35.73) * mm, "end": v(-142.24, 35.73) * mm});
            skLineSegment(sketch, "E314.MirrorCS", {"start": v(-137.03, 72.16) * mm, "end": v(-137.03, 66.96) * mm});
            skLineSegment(sketch, "E315.MirrorCS", {"start": v(-137.03, 4.51) * mm, "end": v(-142.24, 4.51) * mm});
            skLineSegment(sketch, "E316.MirrorCS", {"start": v(-142.24, -5.9) * mm, "end": v(-142.24, -0.69) * mm});
            skLineSegment(sketch, "E317.MirrorCS", {"start": v(-142.24, 51.35) * mm, "end": v(-137.03, 51.35) * mm});
            skLineSegment(sketch, "E318.MirrorCS", {"start": v(-142.24, 46.14) * mm, "end": v(-142.24, 51.35) * mm});
            skLineSegment(sketch, "E319.MirrorCS", {"start": v(-137.03, 82.57) * mm, "end": v(-137.03, 77.36) * mm});
            skLineSegment(sketch, "E320.MirrorCS", {"start": v(-142.24, 66.96) * mm, "end": v(-142.24, 72.16) * mm});
            skLineSegment(sketch, "E321.MirrorCS", {"start": v(-142.24, 40.94) * mm, "end": v(-137.03, 40.94) * mm});
            skLineSegment(sketch, "E322.MirrorCS", {"start": v(-137.03, -21.5) * mm, "end": v(-137.03, -26.7) * mm});
            skLineSegment(sketch, "E323.MirrorCS", {"start": v(-142.24, -21.5) * mm, "end": v(-137.03, -21.5) * mm});
            skLineSegment(sketch, "E324.MirrorCS", {"start": v(-142.24, 61.76) * mm, "end": v(-137.03, 61.76) * mm});
            skLineSegment(sketch, "E325.MirrorCS", {"start": v(-142.24, -11.1) * mm, "end": v(-137.03, -11.1) * mm});
            skLineSegment(sketch, "E326.MirrorCS", {"start": v(-142.24, 30.53) * mm, "end": v(-137.03, 30.53) * mm});
            skLineSegment(sketch, "E327.MirrorCS", {"start": v(-142.24, 4.51) * mm, "end": v(-142.24, 9.72) * mm});
            skLineSegment(sketch, "E328.MirrorCS", {"start": v(-137.03, -5.9) * mm, "end": v(-142.24, -5.9) * mm});
            skLineSegment(sketch, "E329.MirrorCS", {"start": v(-142.24, 20.13) * mm, "end": v(-137.03, 20.13) * mm});
            skLineSegment(sketch, "E330.MirrorCS", {"start": v(-142.24, 77.36) * mm, "end": v(-142.24, 82.57) * mm});
            skLineSegment(sketch, "E331.MirrorCS", {"start": v(-142.24, 98.35) * mm, "end": v(-137.03, 98.35) * mm});
            skLineSegment(sketch, "E332.MirrorCS", {"start": v(-137.03, -0.69) * mm, "end": v(-137.03, -5.9) * mm});
            skLineSegment(sketch, "E333.MirrorCS", {"start": v(-142.24, 35.73) * mm, "end": v(-142.24, 40.94) * mm});
            skLineSegment(sketch, "E334.MirrorCS", {"start": v(-137.03, 46.14) * mm, "end": v(-142.24, 46.14) * mm});
            skLineSegment(sketch, "E335.MirrorCS", {"start": v(-137.03, 40.94) * mm, "end": v(-137.03, 35.73) * mm});
            skLineSegment(sketch, "E336.MirrorCS", {"start": v(-137.03, -26.7) * mm, "end": v(-142.24, -26.7) * mm});
            skLineSegment(sketch, "E337.MirrorCS", {"start": v(-142.24, -31.91) * mm, "end": v(-137.03, -31.91) * mm});
            skLineSegment(sketch, "E338.MirrorCS", {"start": v(-137.03, 30.53) * mm, "end": v(-137.03, 25.33) * mm});
            skLineSegment(sketch, "E339.MirrorCS", {"start": v(-137.03, -16.3) * mm, "end": v(-142.24, -16.3) * mm});
            skLineSegment(sketch, "E340.MirrorCS", {"start": v(-137.03, -11.1) * mm, "end": v(-137.03, -16.3) * mm});
            skLineSegment(sketch, "E341.MirrorCS", {"start": v(-137.03, 77.36) * mm, "end": v(-142.24, 77.36) * mm});
            skLineSegment(sketch, "E342.MirrorCS", {"start": v(-142.24, 14.92) * mm, "end": v(-142.24, 20.13) * mm});
            skLineSegment(sketch, "E343.MirrorCS", {"start": v(-137.03, -41.16) * mm, "end": v(-142.24, -41.16) * mm});
            skLineSegment(sketch, "E344.MirrorCS", {"start": v(-142.24, -16.3) * mm, "end": v(-142.24, -11.1) * mm});
            skLineSegment(sketch, "E345.MirrorCS", {"start": v(-142.24, 56.55) * mm, "end": v(-142.24, 61.76) * mm});
            skLineSegment(sketch, "E346.MirrorCS", {"start": v(-137.03, 56.55) * mm, "end": v(-142.24, 56.55) * mm});
            skLineSegment(sketch, "E347.MirrorCS", {"start": v(-137.03, 87.77) * mm, "end": v(-142.24, 87.77) * mm});
            skLineSegment(sketch, "E348.MirrorCS", {"start": v(-137.03, 61.76) * mm, "end": v(-137.03, 56.55) * mm});
            skLineSegment(sketch, "E349.MirrorCS", {"start": v(-142.24, 25.33) * mm, "end": v(-142.24, 30.53) * mm});
            skLineSegment(sketch, "E350.MirrorCS", {"start": v(-137.03, -31.91) * mm, "end": v(-137.03, -41.16) * mm});
            skLineSegment(sketch, "E351.MirrorCS", {"start": v(-142.24, -41.16) * mm, "end": v(-142.24, -31.91) * mm});
            skLineSegment(sketch, "E352.MirrorCS", {"start": v(-142.24, 87.77) * mm, "end": v(-142.24, 98.35) * mm});
            skLineSegment(sketch, "E353.MirrorCS", {"start": v(-137.03, 98.35) * mm, "end": v(-137.03, 87.77) * mm});
            skSolve(sketch);
        }
        {
            var Q0;
            Q0 = qSketchRegion(id + "F19", true);
            var Q1;
            Q1=makeQuery(id+"F2.opExtrude","SWEPT_FACE",FACE,{"disambiguationData":[OSD([sQuery(id+"F1.wireOp",EDGE,"E12.0")])]});
            extrude(context, id + "F20", {"entities" : qUnion([Q0]), "operationType" : NewBodyOperationType.REMOVE, "endBound" : BoundingType.UP_TO_SURFACE, "oppositeDirection" : true, "endBoundEntityFace" : qUnion([Q1]), "depth" : 25.4 * mm});
        }
        {
            var Q0;
            Q0=makeQuery(id+"F14.opExtrude","SWEPT_FACE",FACE,{"disambiguationData":[OSD([sQuery(id+"F13.wireOp",EDGE,"E260.0.0")])]});
            var sketch = newSketch(context, id + "F21", { "sketchPlane" : qUnion([Q0])});
            skLineSegment(sketch, "E354.0.0", {"start": v(142.24, 53.44) * mm, "end": v(142.24, 61.11) * mm});
            skLineSegment(sketch, "E354.0.1", {"start": v(142.24, 61.11) * mm, "end": v(137.03, 61.11) * mm});
            skLineSegment(sketch, "E354.0.2", {"start": v(137.03, 61.11) * mm, "end": v(137.03, 53.44) * mm});
            skLineSegment(sketch, "E354.0.3", {"start": v(137.03, 53.44) * mm, "end": v(142.24, 53.44) * mm});
            skLineSegment(sketch, "E354.1.0", {"start": v(142.24, 43.03) * mm, "end": v(142.24, 48.23) * mm});
            skLineSegment(sketch, "E354.1.1", {"start": v(142.24, 48.23) * mm, "end": v(137.03, 48.23) * mm});
            skLineSegment(sketch, "E354.1.2", {"start": v(137.03, 48.23) * mm, "end": v(137.03, 43.03) * mm});
            skLineSegment(sketch, "E354.1.3", {"start": v(137.03, 43.03) * mm, "end": v(142.24, 43.03) * mm});
            skLineSegment(sketch, "E354.2.0", {"start": v(142.24, 32.61) * mm, "end": v(142.24, 37.82) * mm});
            skLineSegment(sketch, "E354.2.1", {"start": v(142.24, 37.82) * mm, "end": v(137.03, 37.82) * mm});
            skLineSegment(sketch, "E354.2.2", {"start": v(137.03, 37.82) * mm, "end": v(137.03, 32.61) * mm});
            skLineSegment(sketch, "E354.2.3", {"start": v(137.03, 32.61) * mm, "end": v(142.24, 32.61) * mm});
            skLineSegment(sketch, "E354.3.0", {"start": v(142.24, 22.2) * mm, "end": v(142.24, 27.4) * mm});
            skLineSegment(sketch, "E354.3.1", {"start": v(142.24, 27.4) * mm, "end": v(137.03, 27.4) * mm});
            skLineSegment(sketch, "E354.3.2", {"start": v(137.03, 27.4) * mm, "end": v(137.03, 22.2) * mm});
            skLineSegment(sketch, "E354.3.3", {"start": v(137.03, 22.2) * mm, "end": v(142.24, 22.2) * mm});
            skLineSegment(sketch, "E354.4.0", {"start": v(142.24, 11.78) * mm, "end": v(142.24, 17) * mm});
            skLineSegment(sketch, "E354.4.1", {"start": v(142.24, 17) * mm, "end": v(137.03, 17) * mm});
            skLineSegment(sketch, "E354.4.2", {"start": v(137.03, 17) * mm, "end": v(137.03, 11.78) * mm});
            skLineSegment(sketch, "E354.4.3", {"start": v(137.03, 11.78) * mm, "end": v(142.24, 11.78) * mm});
            skLineSegment(sketch, "E354.5.0", {"start": v(142.24, 1.37) * mm, "end": v(142.24, 6.58) * mm});
            skLineSegment(sketch, "E354.5.1", {"start": v(142.24, 6.58) * mm, "end": v(137.03, 6.58) * mm});
            skLineSegment(sketch, "E354.5.2", {"start": v(137.03, 6.58) * mm, "end": v(137.03, 1.37) * mm});
            skLineSegment(sketch, "E354.5.3", {"start": v(137.03, 1.37) * mm, "end": v(142.24, 1.37) * mm});
            skLineSegment(sketch, "E354.6.0", {"start": v(142.24, -9.04) * mm, "end": v(142.24, -3.84) * mm});
            skLineSegment(sketch, "E354.6.1", {"start": v(142.24, -3.84) * mm, "end": v(137.03, -3.84) * mm});
            skLineSegment(sketch, "E354.6.2", {"start": v(137.03, -3.84) * mm, "end": v(137.03, -9.04) * mm});
            skLineSegment(sketch, "E354.6.3", {"start": v(137.03, -9.04) * mm, "end": v(142.24, -9.04) * mm});
            skLineSegment(sketch, "E354.7.0", {"start": v(142.24, -19.46) * mm, "end": v(142.24, -14.25) * mm});
            skLineSegment(sketch, "E354.7.1", {"start": v(142.24, -14.25) * mm, "end": v(137.03, -14.25) * mm});
            skLineSegment(sketch, "E354.7.2", {"start": v(137.03, -14.25) * mm, "end": v(137.03, -19.46) * mm});
            skLineSegment(sketch, "E354.7.3", {"start": v(137.03, -19.46) * mm, "end": v(142.24, -19.46) * mm});
            skLineSegment(sketch, "E354.8.0", {"start": v(142.24, -29.87) * mm, "end": v(142.24, -24.67) * mm});
            skLineSegment(sketch, "E354.8.1", {"start": v(142.24, -24.67) * mm, "end": v(137.03, -24.67) * mm});
            skLineSegment(sketch, "E354.8.2", {"start": v(137.03, -24.67) * mm, "end": v(137.03, -29.87) * mm});
            skLineSegment(sketch, "E354.8.3", {"start": v(137.03, -29.87) * mm, "end": v(142.24, -29.87) * mm});
            skLineSegment(sketch, "E354.9.0", {"start": v(142.24, -40.29) * mm, "end": v(142.24, -35.08) * mm});
            skLineSegment(sketch, "E354.9.1", {"start": v(142.24, -35.08) * mm, "end": v(137.03, -35.08) * mm});
            skLineSegment(sketch, "E354.9.2", {"start": v(137.03, -35.08) * mm, "end": v(137.03, -40.29) * mm});
            skLineSegment(sketch, "E354.9.3", {"start": v(137.03, -40.29) * mm, "end": v(142.24, -40.29) * mm});
            skLineSegment(sketch, "E354.10.0", {"start": v(142.24, -50.7) * mm, "end": v(142.24, -45.5) * mm});
            skLineSegment(sketch, "E354.10.1", {"start": v(142.24, -45.5) * mm, "end": v(137.03, -45.5) * mm});
            skLineSegment(sketch, "E354.10.2", {"start": v(137.03, -45.5) * mm, "end": v(137.03, -50.7) * mm});
            skLineSegment(sketch, "E354.10.3", {"start": v(137.03, -50.7) * mm, "end": v(142.24, -50.7) * mm});
            skLineSegment(sketch, "E354.11.0", {"start": v(142.24, -61.11) * mm, "end": v(142.24, -55.9) * mm});
            skLineSegment(sketch, "E354.11.1", {"start": v(142.24, -55.9) * mm, "end": v(137.03, -55.9) * mm});
            skLineSegment(sketch, "E354.11.2", {"start": v(137.03, -55.9) * mm, "end": v(137.03, -61.11) * mm});
            skLineSegment(sketch, "E354.11.3", {"start": v(137.03, -61.11) * mm, "end": v(142.24, -61.11) * mm});
            skLineSegment(sketch, "E355.MirrorCS", {"start": v(-142.24, -3.84) * mm, "end": v(-137.03, -3.84) * mm});
            skLineSegment(sketch, "E356.MirrorCS", {"start": v(-137.03, 48.23) * mm, "end": v(-137.03, 43.03) * mm});
            skLineSegment(sketch, "E357.MirrorCS", {"start": v(-142.24, 17) * mm, "end": v(-137.03, 17) * mm});
            skLineSegment(sketch, "E358.MirrorCS", {"start": v(-137.03, 43.03) * mm, "end": v(-142.24, 43.03) * mm});
            skLineSegment(sketch, "E359.MirrorCS", {"start": v(-137.03, -19.46) * mm, "end": v(-142.24, -19.46) * mm});
            skLineSegment(sketch, "E360.MirrorCS", {"start": v(-142.24, -24.67) * mm, "end": v(-137.03, -24.67) * mm});
            skLineSegment(sketch, "E361.MirrorCS", {"start": v(-142.24, -29.87) * mm, "end": v(-142.24, -24.67) * mm});
            skLineSegment(sketch, "E362.MirrorCS", {"start": v(-137.03, -55.9) * mm, "end": v(-137.03, -61.11) * mm});
            skLineSegment(sketch, "E363.MirrorCS", {"start": v(-137.03, -3.84) * mm, "end": v(-137.03, -9.04) * mm});
            skLineSegment(sketch, "E364.MirrorCS", {"start": v(-137.03, -40.29) * mm, "end": v(-142.24, -40.29) * mm});
            skLineSegment(sketch, "E365.MirrorCS", {"start": v(-142.24, -61.11) * mm, "end": v(-142.24, -55.9) * mm});
            skLineSegment(sketch, "E366.MirrorCS", {"start": v(-142.24, -14.25) * mm, "end": v(-137.03, -14.25) * mm});
            skLineSegment(sketch, "E367.MirrorCS", {"start": v(-142.24, 6.58) * mm, "end": v(-137.03, 6.58) * mm});
            skLineSegment(sketch, "E368.MirrorCS", {"start": v(-142.24, -19.46) * mm, "end": v(-142.24, -14.25) * mm});
            skLineSegment(sketch, "E369.MirrorCS", {"start": v(-142.24, 43.03) * mm, "end": v(-142.24, 48.23) * mm});
            skLineSegment(sketch, "E370.MirrorCS", {"start": v(-137.03, 17) * mm, "end": v(-137.03, 11.78) * mm});
            skLineSegment(sketch, "E371.MirrorCS", {"start": v(-142.24, 11.78) * mm, "end": v(-142.24, 17) * mm});
            skLineSegment(sketch, "E372.MirrorCS", {"start": v(-142.24, 27.4) * mm, "end": v(-137.03, 27.4) * mm});
            skLineSegment(sketch, "E373.MirrorCS", {"start": v(-137.03, 1.37) * mm, "end": v(-142.24, 1.37) * mm});
            skLineSegment(sketch, "E374.MirrorCS", {"start": v(-142.24, 32.61) * mm, "end": v(-142.24, 37.82) * mm});
            skLineSegment(sketch, "E375.MirrorCS", {"start": v(-137.03, -50.7) * mm, "end": v(-142.24, -50.7) * mm});
            skLineSegment(sketch, "E376.MirrorCS", {"start": v(-137.03, -24.67) * mm, "end": v(-137.03, -29.87) * mm});
            skLineSegment(sketch, "E377.MirrorCS", {"start": v(-137.03, 6.58) * mm, "end": v(-137.03, 1.37) * mm});
            skLineSegment(sketch, "E378.MirrorCS", {"start": v(-142.24, 1.37) * mm, "end": v(-142.24, 6.58) * mm});
            skLineSegment(sketch, "E379.MirrorCS", {"start": v(-142.24, 37.82) * mm, "end": v(-137.03, 37.82) * mm});
            skLineSegment(sketch, "E380.MirrorCS", {"start": v(-142.24, -50.7) * mm, "end": v(-142.24, -45.5) * mm});
            skLineSegment(sketch, "E381.MirrorCS", {"start": v(-142.24, -9.04) * mm, "end": v(-142.24, -3.84) * mm});
            skLineSegment(sketch, "E382.MirrorCS", {"start": v(-142.24, -45.5) * mm, "end": v(-137.03, -45.5) * mm});
            skLineSegment(sketch, "E383.MirrorCS", {"start": v(-137.03, 53.44) * mm, "end": v(-142.24, 53.44) * mm});
            skLineSegment(sketch, "E384.MirrorCS", {"start": v(-142.24, -35.08) * mm, "end": v(-137.03, -35.08) * mm});
            skLineSegment(sketch, "E385.MirrorCS", {"start": v(-137.03, -35.08) * mm, "end": v(-137.03, -40.29) * mm});
            skLineSegment(sketch, "E386.MirrorCS", {"start": v(-137.03, -61.11) * mm, "end": v(-142.24, -61.11) * mm});
            skLineSegment(sketch, "E387.MirrorCS", {"start": v(-142.24, -40.29) * mm, "end": v(-142.24, -35.08) * mm});
            skLineSegment(sketch, "E388.MirrorCS", {"start": v(-137.03, -9.04) * mm, "end": v(-142.24, -9.04) * mm});
            skLineSegment(sketch, "E389.MirrorCS", {"start": v(-137.03, 22.2) * mm, "end": v(-142.24, 22.2) * mm});
            skLineSegment(sketch, "E390.MirrorCS", {"start": v(-137.03, 27.4) * mm, "end": v(-137.03, 22.2) * mm});
            skLineSegment(sketch, "E391.MirrorCS", {"start": v(-137.03, -14.25) * mm, "end": v(-137.03, -19.46) * mm});
            skLineSegment(sketch, "E392.MirrorCS", {"start": v(-142.24, 48.23) * mm, "end": v(-137.03, 48.23) * mm});
            skLineSegment(sketch, "E393.MirrorCS", {"start": v(-137.03, -29.87) * mm, "end": v(-142.24, -29.87) * mm});
            skLineSegment(sketch, "E394.MirrorCS", {"start": v(-137.03, 11.78) * mm, "end": v(-142.24, 11.78) * mm});
            skLineSegment(sketch, "E395.MirrorCS", {"start": v(-142.24, -55.9) * mm, "end": v(-137.03, -55.9) * mm});
            skLineSegment(sketch, "E396.MirrorCS", {"start": v(-142.24, 22.2) * mm, "end": v(-142.24, 27.4) * mm});
            skLineSegment(sketch, "E397.MirrorCS", {"start": v(-137.03, 32.61) * mm, "end": v(-142.24, 32.61) * mm});
            skLineSegment(sketch, "E398.MirrorCS", {"start": v(-142.24, 61.11) * mm, "end": v(-137.03, 61.11) * mm});
            skLineSegment(sketch, "E399.MirrorCS", {"start": v(-137.03, 37.82) * mm, "end": v(-137.03, 32.61) * mm});
            skLineSegment(sketch, "E400.MirrorCS", {"start": v(-137.03, -45.5) * mm, "end": v(-137.03, -50.7) * mm});
            skLineSegment(sketch, "E401.MirrorCS", {"start": v(-137.03, 61.11) * mm, "end": v(-137.03, 53.44) * mm});
            skLineSegment(sketch, "E402.MirrorCS", {"start": v(-142.24, 53.44) * mm, "end": v(-142.24, 61.11) * mm});
            skSolve(sketch);
        }
        {
            var Q0;
            Q0 = qSketchRegion(id + "F21", true);
            extrude(context, id + "F22", {"entities" : qUnion([Q0]), "operationType" : NewBodyOperationType.REMOVE, "endBound" : BoundingType.UP_TO_NEXT, "oppositeDirection" : true, "depth" : 25.4 * mm});
        }
        {
            var Q0;
            Q0=makeQuery(id+"F16.opExtrude","SWEPT_BODY",BODY,{"disambiguationData":[OSD([sQuery(id+"F15.wireOp",EDGE,"E263"),sQuery(id+"F15.wireOp",EDGE,"E264"),sQuery(id+"F15.wireOp",EDGE,"E265"),sQuery(id+"F15.wireOp",EDGE,"E266"),sQuery(id+"F15.wireOp",EDGE,"E267"),sQuery(id+"F15.wireOp",EDGE,"E268"),sQuery(id+"F15.wireOp",EDGE,"E270.1.0.0"),sQuery(id+"F15.wireOp",EDGE,"E270.1.0.1"),sQuery(id+"F15.wireOp",EDGE,"E270.1.0.2"),sQuery(id+"F15.wireOp",EDGE,"E270.1.0.3"),sQuery(id+"F15.wireOp",EDGE,"E270.2.0.0"),sQuery(id+"F15.wireOp",EDGE,"E270.2.0.1"),sQuery(id+"F15.wireOp",EDGE,"E270.2.0.2"),sQuery(id+"F15.wireOp",EDGE,"E270.2.0.3"),sQuery(id+"F15.wireOp",EDGE,"E270.3.0.0"),sQuery(id+"F15.wireOp",EDGE,"E270.3.0.1"),sQuery(id+"F15.wireOp",EDGE,"E270.3.0.2"),sQuery(id+"F15.wireOp",EDGE,"E270.3.0.3"),sQuery(id+"F15.wireOp",EDGE,"E270.4.0.0"),sQuery(id+"F15.wireOp",EDGE,"E270.4.0.1"),sQuery(id+"F15.wireOp",EDGE,"E270.4.0.2"),sQuery(id+"F15.wireOp",EDGE,"E270.4.0.3"),sQuery(id+"F15.wireOp",EDGE,"E270.5.0.0"),sQuery(id+"F15.wireOp",EDGE,"E270.5.0.1"),sQuery(id+"F15.wireOp",EDGE,"E270.5.0.2"),sQuery(id+"F15.wireOp",EDGE,"E270.5.0.3"),sQuery(id+"F15.wireOp",EDGE,"E270.6.0.0"),sQuery(id+"F15.wireOp",EDGE,"E270.6.0.1"),sQuery(id+"F15.wireOp",EDGE,"E270.6.0.2"),sQuery(id+"F15.wireOp",EDGE,"E270.6.0.3"),sQuery(id+"F15.wireOp",EDGE,"E270.7.0.0"),sQuery(id+"F15.wireOp",EDGE,"E270.7.0.1"),sQuery(id+"F15.wireOp",EDGE,"E270.7.0.2"),sQuery(id+"F15.wireOp",EDGE,"E270.7.0.3"),sQuery(id+"F15.wireOp",EDGE,"E270.8.0.0"),sQuery(id+"F15.wireOp",EDGE,"E270.8.0.1"),sQuery(id+"F15.wireOp",EDGE,"E270.8.0.2"),sQuery(id+"F15.wireOp",EDGE,"E270.8.0.3"),sQuery(id+"F15.wireOp",EDGE,"E270.9.0.0"),sQuery(id+"F15.wireOp",EDGE,"E270.9.0.1"),sQuery(id+"F15.wireOp",EDGE,"E270.9.0.2"),sQuery(id+"F15.wireOp",EDGE,"E270.9.0.3"),sQuery(id+"F15.wireOp",EDGE,"E270.10.0.0"),sQuery(id+"F15.wireOp",EDGE,"E270.10.0.1"),sQuery(id+"F15.wireOp",EDGE,"E270.10.0.2"),sQuery(id+"F15.wireOp",EDGE,"E270.10.0.3"),sQuery(id+"F15.wireOp",EDGE,"E270.11.0.2"),sQuery(id+"F15.wireOp",EDGE,"E270.11.0.3"),sQuery(id+"F15.wireOp",EDGE,"E272"),sQuery(id+"F15.wireOp",EDGE,"E273"),sQuery(id+"F15.wireOp",EDGE,"E274"),sQuery(id+"F15.wireOp",EDGE,"E275"),sQuery(id+"F15.wireOp",EDGE,"E276"),sQuery(id+"F15.wireOp",EDGE,"E277"),sQuery(id+"F15.wireOp",EDGE,"E278"),sQuery(id+"F15.wireOp",EDGE,"E280"),sQuery(id+"F15.wireOp",EDGE,"E281"),sQuery(id+"F15.wireOp",EDGE,"E282"),sQuery(id+"F15.wireOp",EDGE,"E283"),sQuery(id+"F15.wireOp",EDGE,"E284.1.0.0"),sQuery(id+"F15.wireOp",EDGE,"E284.1.0.1"),sQuery(id+"F15.wireOp",EDGE,"E284.1.0.2"),sQuery(id+"F15.wireOp",EDGE,"E284.1.0.3"),sQuery(id+"F15.wireOp",EDGE,"E284.2.0.0"),sQuery(id+"F15.wireOp",EDGE,"E284.2.0.1"),sQuery(id+"F15.wireOp",EDGE,"E284.2.0.2"),sQuery(id+"F15.wireOp",EDGE,"E284.2.0.3"),sQuery(id+"F15.wireOp",EDGE,"E284.3.0.0"),sQuery(id+"F15.wireOp",EDGE,"E284.3.0.1"),sQuery(id+"F15.wireOp",EDGE,"E284.3.0.2"),sQuery(id+"F15.wireOp",EDGE,"E284.3.0.3"),sQuery(id+"F15.wireOp",EDGE,"E284.4.0.0"),sQuery(id+"F15.wireOp",EDGE,"E284.4.0.1"),sQuery(id+"F15.wireOp",EDGE,"E284.4.0.2"),sQuery(id+"F15.wireOp",EDGE,"E284.4.0.3"),sQuery(id+"F15.wireOp",EDGE,"E284.5.0.0"),sQuery(id+"F15.wireOp",EDGE,"E284.5.0.1"),sQuery(id+"F15.wireOp",EDGE,"E284.5.0.2"),sQuery(id+"F15.wireOp",EDGE,"E284.5.0.3"),sQuery(id+"F15.wireOp",EDGE,"E284.6.0.0"),sQuery(id+"F15.wireOp",EDGE,"E284.6.0.1"),sQuery(id+"F15.wireOp",EDGE,"E284.6.0.2"),sQuery(id+"F15.wireOp",EDGE,"E284.6.0.3"),sQuery(id+"F15.wireOp",EDGE,"E284.7.0.0"),sQuery(id+"F15.wireOp",EDGE,"E284.7.0.1"),sQuery(id+"F15.wireOp",EDGE,"E284.7.0.2"),sQuery(id+"F15.wireOp",EDGE,"E284.7.0.3"),sQuery(id+"F15.wireOp",EDGE,"E284.8.0.0"),sQuery(id+"F15.wireOp",EDGE,"E284.8.0.1"),sQuery(id+"F15.wireOp",EDGE,"E284.8.0.2"),sQuery(id+"F15.wireOp",EDGE,"E284.8.0.3"),sQuery(id+"F15.wireOp",EDGE,"E284.9.0.0"),sQuery(id+"F15.wireOp",EDGE,"E284.9.0.1"),sQuery(id+"F15.wireOp",EDGE,"E284.9.0.2"),sQuery(id+"F15.wireOp",EDGE,"E284.9.0.3"),sQuery(id+"F15.wireOp",EDGE,"E284.10.0.0"),sQuery(id+"F15.wireOp",EDGE,"E284.10.0.1"),sQuery(id+"F15.wireOp",EDGE,"E284.10.0.2"),sQuery(id+"F15.wireOp",EDGE,"E284.10.0.3"),sQuery(id+"F15.wireOp",EDGE,"E285"),sQuery(id+"F15.wireOp",EDGE,"E286"),sQuery(id+"F15.wireOp",EDGE,"E287"),sQuery(id+"F15.wireOp",EDGE,"E288")])]});
            transform(context, id + "F23", {"entities" : qUnion([Q0]), "transformType" : TransformType.TRANSLATION_3D, "dx" : -279.27 * mm, "dy" : 0 * mm, "dz" : 0 * mm, "makeCopy" : true});
        }
        {
            var Q0;
            Q0=makeQuery(id+"F2.opExtrude","SWEPT_FACE",FACE,{"disambiguationData":[OSD([sQuery(id+"F1.wireOp",EDGE,"E12.2")])]});
            var sketch = newSketch(context, id + "F24", { "sketchPlane" : qUnion([Q0])});
            skPoint(sketch, "E403.0", {"position": v(0, 28.6) * mm});
            skLineSegment(sketch, "E404.bottom", {"start": v(14.15, -24.74) * mm, "end": v(-14.15, -24.74) * mm});
            skLineSegment(sketch, "E404.top", {"start": v(14.15, 81.94) * mm, "end": v(-14.15, 81.94) * mm});
            skLineSegment(sketch, "E404.left", {"start": v(20.5, -18.4) * mm, "end": v(20.5, 75.59) * mm});
            skLineSegment(sketch, "E404.right", {"start": v(-20.5, -18.4) * mm, "end": v(-20.5, 75.59) * mm});
            skPoint(sketch, "E405.visualSharp", {"position": v(20.5, 81.94) * mm});
            skArc(sketch, "E405.filletArc", {"start": v(20.5, 75.59) * mm, "mid": v(18.64, 80.08) * mm, "end": v(14.15, 81.94) * mm});
            skPoint(sketch, "E406.visualSharp", {"position": v(20.5, -24.74) * mm});
            skArc(sketch, "E406.filletArc", {"start": v(14.15, -24.74) * mm, "mid": v(18.64, -22.88) * mm, "end": v(20.5, -18.4) * mm});
            skPoint(sketch, "E407.visualSharp", {"position": v(-20.5, -24.74) * mm});
            skArc(sketch, "E407.filletArc", {"start": v(-20.5, -18.4) * mm, "mid": v(-18.64, -22.88) * mm, "end": v(-14.15, -24.74) * mm});
            skPoint(sketch, "E408.visualSharp", {"position": v(-20.5, 81.94) * mm});
            skArc(sketch, "E408.filletArc", {"start": v(-14.15, 81.94) * mm, "mid": v(-18.64, 80.08) * mm, "end": v(-20.5, 75.59) * mm});
            skLineSegment(sketch, "E409.1.0.0", {"start": v(60.19, 81.94) * mm, "end": v(31.89, 81.94) * mm});
            skArc(sketch, "E409.1.0.1", {"start": v(66.54, 75.59) * mm, "mid": v(64.68, 80.08) * mm, "end": v(60.19, 81.94) * mm});
            skLineSegment(sketch, "E409.1.0.2", {"start": v(66.54, -18.4) * mm, "end": v(66.54, 75.59) * mm});
            skArc(sketch, "E409.1.0.3", {"start": v(60.19, -24.74) * mm, "mid": v(64.68, -22.88) * mm, "end": v(66.54, -18.4) * mm});
            skLineSegment(sketch, "E409.1.0.4", {"start": v(60.19, -24.74) * mm, "end": v(31.89, -24.74) * mm});
            skArc(sketch, "E409.1.0.5", {"start": v(25.54, -18.4) * mm, "mid": v(27.4, -22.88) * mm, "end": v(31.89, -24.74) * mm});
            skLineSegment(sketch, "E409.1.0.6", {"start": v(25.54, -18.4) * mm, "end": v(25.54, 75.59) * mm});
            skArc(sketch, "E409.1.0.7", {"start": v(31.89, 81.94) * mm, "mid": v(27.4, 80.08) * mm, "end": v(25.54, 75.59) * mm});
            skLineSegment(sketch, "E409.2.0.2", {"start": v(112.58, -1.57) * mm, "end": v(112.58, 58.76) * mm});
            skLineSegment(sketch, "E409.2.0.6", {"start": v(71.58, -1.57) * mm, "end": v(71.58, 58.76) * mm});
            skLineSegment(sketch, "E409.direction1", {"start": v(-14.15, -24.74) * mm, "end": v(31.89, -24.74) * mm, "construction": true});
            skLineSegment(sketch, "E410.bottom", {"start": v(131.76, -33.32) * mm, "end": v(-131.76, -33.32) * mm, "construction": true});
            skLineSegment(sketch, "E410.top", {"start": v(131.76, 90.5) * mm, "end": v(-131.76, 90.5) * mm, "construction": true});
            skLineSegment(sketch, "E410.left", {"start": v(131.76, -33.32) * mm, "end": v(131.76, 90.5) * mm, "construction": true});
            skLineSegment(sketch, "E410.right", {"start": v(-131.76, -33.32) * mm, "end": v(-131.76, 90.5) * mm, "construction": true});
            skLineSegment(sketch, "E411", {"start": v(106.23, 65.1) * mm, "end": v(77.93, 65.1) * mm});
            skLineSegment(sketch, "E412", {"start": v(106.23, -7.92) * mm, "end": v(77.93, -7.92) * mm});
            skPoint(sketch, "E413.orphan", {"position": v(112.58, 75.59) * mm});
            skPoint(sketch, "E414.orphan", {"position": v(71.58, -18.4) * mm});
            skLineSegment(sketch, "E415", {"start": v(0, 28.6) * mm, "end": v(71.58, 28.6) * mm, "construction": true});
            skPoint(sketch, "E416.visualSharp", {"position": v(71.58, 65.1) * mm});
            skArc(sketch, "E416.filletArc", {"start": v(77.93, 65.1) * mm, "mid": v(73.43, 63.25) * mm, "end": v(71.58, 58.76) * mm});
            skPoint(sketch, "E417.visualSharp", {"position": v(112.58, 65.1) * mm});
            skArc(sketch, "E417.filletArc", {"start": v(112.58, 58.76) * mm, "mid": v(110.72, 63.25) * mm, "end": v(106.23, 65.1) * mm});
            skPoint(sketch, "E418.visualSharp", {"position": v(112.58, -7.92) * mm});
            skArc(sketch, "E418.filletArc", {"start": v(106.23, -7.92) * mm, "mid": v(110.72, -6.06) * mm, "end": v(112.58, -1.57) * mm});
            skPoint(sketch, "E419.visualSharp", {"position": v(71.58, -7.92) * mm});
            skArc(sketch, "E419.filletArc", {"start": v(71.58, -1.57) * mm, "mid": v(73.43, -6.06) * mm, "end": v(77.93, -7.92) * mm});
            skCircle(sketch, "E420", {"center": v(78.58, 77.01) * mm, "radius": 1.59 * mm});
            skLineSegment(sketch, "E421", {"start": v(92.08, 65.1) * mm, "end": v(92.08, -7.92) * mm, "construction": true});
            skLineSegment(sketch, "E422", {"start": v(71.58, 28.6) * mm, "end": v(112.58, 28.6) * mm, "construction": true});
            skCircle(sketch, "E423.MirrorC", {"center": v(105.57, 77.01) * mm, "radius": 1.59 * mm});
            skCircle(sketch, "E424.MirrorC", {"center": v(105.57, -19.82) * mm, "radius": 1.59 * mm});
            skCircle(sketch, "E425.MirrorC", {"center": v(78.58, -19.82) * mm, "radius": 1.59 * mm});
            skArc(sketch, "E426.MirrorCS", {"start": v(-77.93, 65.1) * mm, "mid": v(-73.43, 63.25) * mm, "end": v(-71.58, 58.76) * mm});
            skCircle(sketch, "E427.MirrorC", {"center": v(-78.58, 77.01) * mm, "radius": 1.59 * mm});
            skArc(sketch, "E428.MirrorCS", {"start": v(-106.23, -7.92) * mm, "mid": v(-110.72, -6.06) * mm, "end": v(-112.58, -1.57) * mm});
            skCircle(sketch, "E429.MirrorC", {"center": v(-78.58, -19.82) * mm, "radius": 1.59 * mm});
            skArc(sketch, "E430.MirrorCS", {"start": v(-71.58, -1.57) * mm, "mid": v(-73.43, -6.06) * mm, "end": v(-77.93, -7.92) * mm});
            skCircle(sketch, "E431.MirrorC", {"center": v(-105.57, 77.01) * mm, "radius": 1.59 * mm});
            skCircle(sketch, "E432.MirrorC", {"center": v(-105.57, -19.82) * mm, "radius": 1.59 * mm});
            skArc(sketch, "E433.MirrorCS", {"start": v(-112.58, 58.76) * mm, "mid": v(-110.72, 63.25) * mm, "end": v(-106.23, 65.1) * mm});
            skPoint(sketch, "E434.MirrorP", {"position": v(-112.58, 75.59) * mm});
            skLineSegment(sketch, "E435.MirrorCS", {"start": v(-60.19, 81.94) * mm, "end": v(-31.89, 81.94) * mm});
            skArc(sketch, "E436.MirrorCS", {"start": v(-66.54, 75.59) * mm, "mid": v(-64.68, 80.08) * mm, "end": v(-60.19, 81.94) * mm});
            skPoint(sketch, "E437.MirrorP", {"position": v(-112.58, -7.92) * mm});
            skLineSegment(sketch, "E438.MirrorCS", {"start": v(-66.54, -18.4) * mm, "end": v(-66.54, 75.59) * mm});
            skPoint(sketch, "E439.MirrorP", {"position": v(-71.58, -7.92) * mm});
            skArc(sketch, "E440.MirrorCS", {"start": v(-60.19, -24.74) * mm, "mid": v(-64.68, -22.88) * mm, "end": v(-66.54, -18.4) * mm});
            skPoint(sketch, "E441.MirrorP", {"position": v(-71.58, -18.4) * mm});
            skLineSegment(sketch, "E442.MirrorCS", {"start": v(-112.58, -1.57) * mm, "end": v(-112.58, 58.76) * mm});
            skLineSegment(sketch, "E443.MirrorCS", {"start": v(-60.19, -24.74) * mm, "end": v(-31.89, -24.74) * mm});
            skLineSegment(sketch, "E444.MirrorCS", {"start": v(-106.23, 65.1) * mm, "end": v(-77.93, 65.1) * mm});
            skLineSegment(sketch, "E445.MirrorCS", {"start": v(-71.58, 28.6) * mm, "end": v(-112.58, 28.6) * mm, "construction": true});
            skLineSegment(sketch, "E446.MirrorCS", {"start": v(-92.08, 65.1) * mm, "end": v(-92.08, -7.92) * mm, "construction": true});
            skLineSegment(sketch, "E447.MirrorCS", {"start": v(-106.23, -7.92) * mm, "end": v(-77.93, -7.92) * mm});
            skPoint(sketch, "E448.MirrorP", {"position": v(-71.58, 65.1) * mm});
            skLineSegment(sketch, "E449.MirrorCS", {"start": v(-71.58, -1.57) * mm, "end": v(-71.58, 58.76) * mm});
            skArc(sketch, "E450.MirrorCS", {"start": v(-25.54, -18.4) * mm, "mid": v(-27.4, -22.88) * mm, "end": v(-31.89, -24.74) * mm});
            skArc(sketch, "E451.MirrorCS", {"start": v(-31.89, 81.94) * mm, "mid": v(-27.4, 80.08) * mm, "end": v(-25.54, 75.59) * mm});
            skLineSegment(sketch, "E452.MirrorCS", {"start": v(-25.54, -18.4) * mm, "end": v(-25.54, 75.59) * mm});
            skPoint(sketch, "E453.MirrorP", {"position": v(-112.58, 65.1) * mm});
            skSolve(sketch);
        }
        {
            var Q0;
            Q0 = qSketchRegion(id + "F24", true);
            extrude(context, id + "F25", {"entities" : qUnion([Q0]), "operationType" : NewBodyOperationType.REMOVE, "endBound" : BoundingType.UP_TO_NEXT, "oppositeDirection" : true, "depth" : 25.4 * mm});
        }
        {
            var Q0;
            Q0=makeQuery(id+"F25.boolean.opBoolean","COPY",FACE,{"derivedFrom":makeQuery(id+"F25.opExtrude","SWEPT_FACE",FACE,{"disambiguationData":[OSD([sQuery(id+"F24.wireOp",EDGE,"E409.2.0.6")])]})});
            var sketch = newSketch(context, id + "F26", { "sketchPlane" : qUnion([Q0])});
            skLineSegment(sketch, "E454.0", {"start": v(55.91, 2.6) * mm, "end": v(-45.24, 2.6) * mm});
            skLineSegment(sketch, "E454.1", {"start": v(55.91, 99.1) * mm, "end": v(55.91, 2.6) * mm});
            skLineSegment(sketch, "E454.2", {"start": v(-61.11, 13.97) * mm, "end": v(-61.11, 2.6) * mm, "construction": true});
            skLineSegment(sketch, "E454.3", {"start": v(-45.24, 26.84) * mm, "end": v(43.9, 99.1) * mm});
            skLineSegment(sketch, "E454.4", {"start": v(43.9, 99.1) * mm, "end": v(55.91, 99.1) * mm});
            skPoint(sketch, "E455.orphan", {"position": v(61.11, 99.1) * mm});
            skPoint(sketch, "E456.orphan", {"position": v(45.34, 100.26) * mm});
            skPoint(sketch, "E457.orphan", {"position": v(42.06, 99.1) * mm});
            skPoint(sketch, "E458.orphan", {"position": v(61.11, 2.6) * mm});
            skPoint(sketch, "E459.orphan", {"position": v(-61.11, -2.6) * mm});
            skPoint(sketch, "E460.orphan", {"position": v(-63.04, 12.41) * mm});
            skPoint(sketch, "E461.orphan", {"position": v(-61.11, 16.45) * mm});
            skLineSegment(sketch, "E462", {"start": v(-45.24, 2.6) * mm, "end": v(-45.24, 26.84) * mm});
            skSolve(sketch);
        }
        {
            var Q0;
            Q0 = qSketchRegion(id + "F26", true);
            extrude(context, id + "F27", {"entities" : qUnion([Q0]), "oppositeDirection" : true, "depth" : 5.2 * mm});
        }
        {
            var Q0;
            Q0=makeQuery(id+"F14.opExtrude","SWEPT_FACE",FACE,{"disambiguationData":[OSD([sQuery(id+"F13.wireOp",EDGE,"E260.0.1")])]});
            var sketch = newSketch(context, id + "F28", { "sketchPlane" : qUnion([Q0])});
            skLineSegment(sketch, "E463.0", {"start": v(-137.03, 99.1) * mm, "end": v(137.03, 99.1) * mm});
            skLineSegment(sketch, "E463.1", {"start": v(-137.03, 99.1) * mm, "end": v(-137.03, 31.17) * mm});
            skLineSegment(sketch, "E463.2", {"start": v(-98.93, 2.6) * mm, "end": v(-60.19, 2.6) * mm});
            skLineSegment(sketch, "E463.3", {"start": v(137.03, 99.1) * mm, "end": v(137.03, 31.17) * mm});
            skPoint(sketch, "E464.orphan", {"position": v(-137.03, 104.3) * mm});
            skPoint(sketch, "E465.orphan", {"position": v(-137.03, -2.6) * mm});
            skPoint(sketch, "E466.orphan", {"position": v(137.03, -2.6) * mm});
            skPoint(sketch, "E467.orphan", {"position": v(137.03, 104.3) * mm});
            skLineSegment(sketch, "E468", {"start": v(-137.03, 31.17) * mm, "end": v(-105.28, 31.17) * mm});
            skLineSegment(sketch, "E469", {"start": v(-98.93, 24.82) * mm, "end": v(-98.93, 2.6) * mm});
            skLineSegment(sketch, "E470", {"start": v(-60.19, 2.6) * mm, "end": v(-60.19, 24.82) * mm});
            skLineSegment(sketch, "E471", {"start": v(-53.84, 31.17) * mm, "end": v(53.84, 31.17) * mm});
            skLineSegment(sketch, "E472", {"start": v(60.19, 24.83) * mm, "end": v(60.19, 2.6) * mm});
            skLineSegment(sketch, "E473", {"start": v(137.03, 31.17) * mm, "end": v(105.28, 31.17) * mm});
            skLineSegment(sketch, "E474", {"start": v(98.93, 24.83) * mm, "end": v(98.93, 2.6) * mm});
            skLineSegment(sketch, "E475", {"start": v(0, 31.17) * mm, "end": v(0, 2.6) * mm, "construction": true});
            skPoint(sketch, "E476.orphan", {"position": v(-137.03, 2.6) * mm});
            skLineSegment(sketch, "E477.trimOffspring", {"start": v(60.19, 2.6) * mm, "end": v(98.93, 2.6) * mm});
            skPoint(sketch, "E478.orphan", {"position": v(137.03, 2.6) * mm});
            skPoint(sketch, "E479.visualSharp", {"position": v(-98.93, 31.17) * mm});
            skArc(sketch, "E479.filletArc", {"start": v(-98.93, 24.82) * mm, "mid": v(-100.8, 29.32) * mm, "end": v(-105.28, 31.17) * mm});
            skPoint(sketch, "E480.visualSharp", {"position": v(-60.19, 31.18) * mm});
            skArc(sketch, "E480.filletArc", {"start": v(-53.84, 31.17) * mm, "mid": v(-58.33, 29.32) * mm, "end": v(-60.19, 24.82) * mm});
            skPoint(sketch, "E481.visualSharp", {"position": v(60.19, 31.17) * mm});
            skArc(sketch, "E481.filletArc", {"start": v(60.19, 24.83) * mm, "mid": v(58.33, 29.32) * mm, "end": v(53.84, 31.18) * mm});
            skPoint(sketch, "E482.visualSharp", {"position": v(98.93, 31.18) * mm});
            skArc(sketch, "E482.filletArc", {"start": v(105.28, 31.18) * mm, "mid": v(100.8, 29.32) * mm, "end": v(98.93, 24.83) * mm});
            skSolve(sketch);
        }
        {
            var Q0;
            Q0 = qSketchRegion(id + "F28", true);
            extrude(context, id + "F29", {"entities" : qUnion([Q0]), "oppositeDirection" : true, "depth" : 5.2 * mm});
        }
    });
